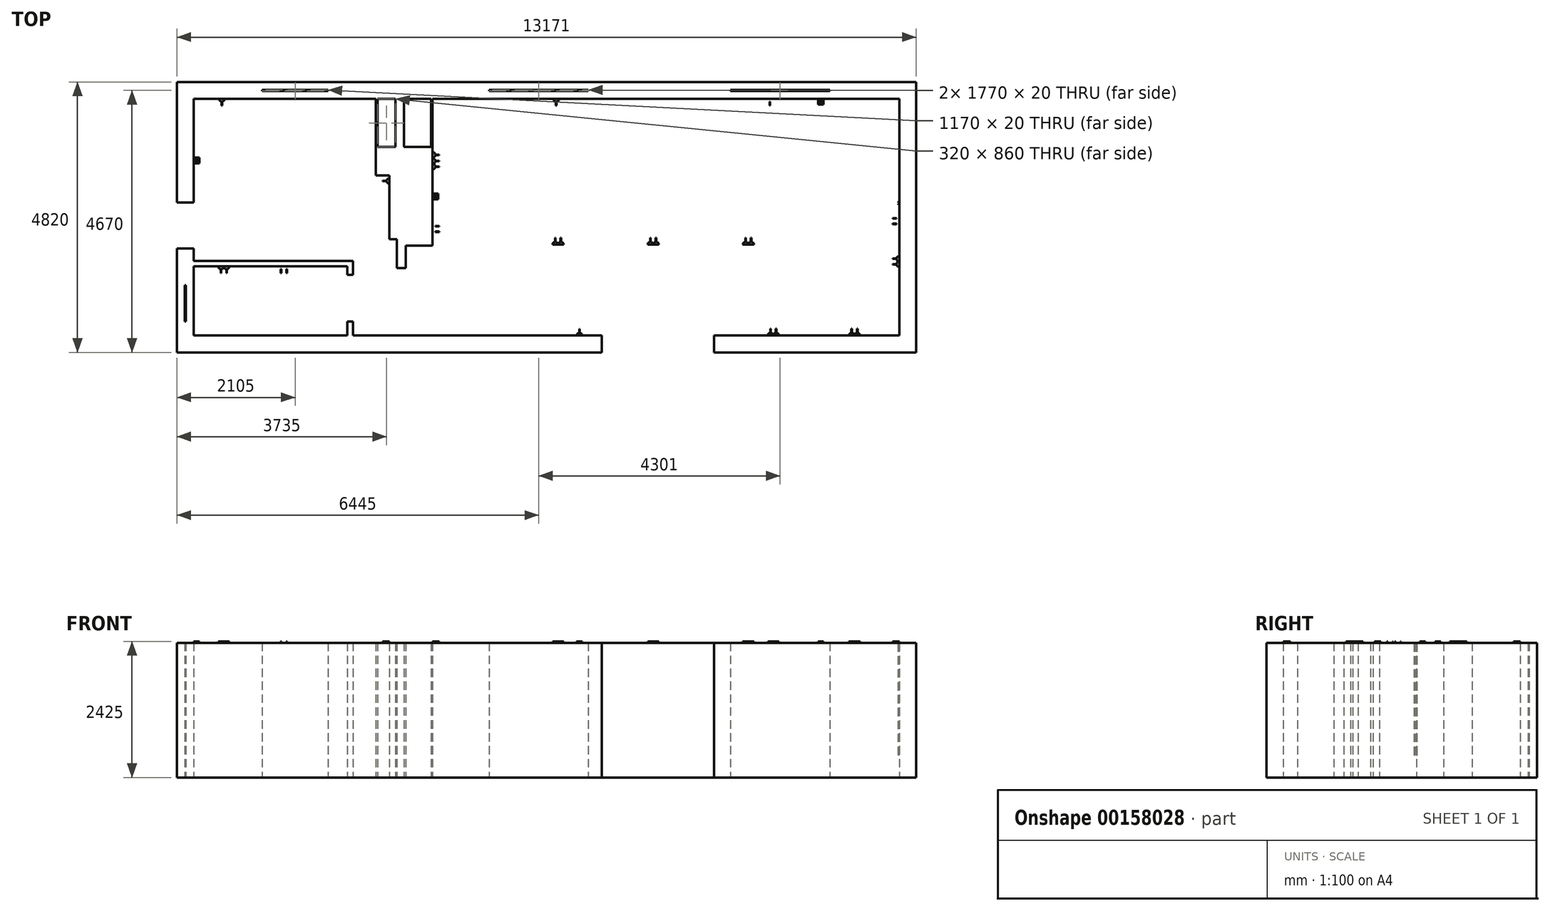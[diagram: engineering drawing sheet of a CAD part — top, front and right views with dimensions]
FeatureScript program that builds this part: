
annotation { "Feature Type Name" : "Feature", "Feature Type Description" : "" }
export const myFeature = defineFeature(function(context is Context, id is Id, definition is map)
    precondition{}
    {
        {
            var Q0;
            Q0=qCreatedBy(makeId("Top.planeOp"),FACE);
            var sketch = newSketch(context, id + "F0", { "sketchPlane" : qUnion([Q0])});
            skLineSegment(sketch, "E0", {"start": v(-4269.88, 1654.6) * mm, "end": v(-3049.88, 1654.6) * mm});
            skLineSegment(sketch, "E1", {"start": v(-3049.88, 1654.6) * mm, "end": v(-3049.88, 1954.6) * mm});
            skLineSegment(sketch, "E2", {"start": v(-3049.88, 1954.6) * mm, "end": v(-4569.88, 1954.6) * mm});
            skLineSegment(sketch, "E3", {"start": v(-4569.88, 1954.6) * mm, "end": v(-4569.88, -195.4) * mm});
            skLineSegment(sketch, "E4", {"start": v(-4569.88, -195.4) * mm, "end": v(-4269.88, -195.4) * mm});
            skLineSegment(sketch, "E5", {"start": v(-4269.88, -195.4) * mm, "end": v(-4269.88, 1654.6) * mm});
            skLineSegment(sketch, "E6", {"start": v(-674.88, 794.6) * mm, "end": v(-674.88, 1654.6) * mm});
            skLineSegment(sketch, "E7", {"start": v(-674.88, 1654.6) * mm, "end": v(-1879.88, 1654.6) * mm});
            skLineSegment(sketch, "E8", {"start": v(-1879.88, 1654.6) * mm, "end": v(-1879.88, 1954.6) * mm});
            skLineSegment(sketch, "E9", {"start": v(-1879.88, 1954.6) * mm, "end": v(990.12, 1954.6) * mm});
            skLineSegment(sketch, "E10", {"start": v(990.12, 1954.6) * mm, "end": v(990.12, 1654.6) * mm});
            skLineSegment(sketch, "E11", {"start": v(990.12, 1654.6) * mm, "end": v(-524.88, 1654.6) * mm});
            skLineSegment(sketch, "E12", {"start": v(-524.88, 1654.6) * mm, "end": v(-524.88, 794.6) * mm});
            skLineSegment(sketch, "E13", {"start": v(-674.88, 794.6) * mm, "end": v(-1024.88, 794.6) * mm});
            skLineSegment(sketch, "E14", {"start": v(-1024.88, 794.6) * mm, "end": v(-1024.88, 289.6) * mm});
            skLineSegment(sketch, "E15", {"start": v(-1024.88, 289.6) * mm, "end": v(-784.88, 289.6) * mm});
            skLineSegment(sketch, "E16", {"start": v(-784.88, 289.6) * mm, "end": v(-784.88, -850.4) * mm});
            skLineSegment(sketch, "E17", {"start": v(-784.88, -850.4) * mm, "end": v(-654.88, -850.4) * mm});
            skLineSegment(sketch, "E18", {"start": v(-654.88, -850.4) * mm, "end": v(-654.88, -1365.4) * mm});
            skLineSegment(sketch, "E19", {"start": v(-654.88, -1365.4) * mm, "end": v(-494.88, -1365.4) * mm});
            skLineSegment(sketch, "E20", {"start": v(-494.88, -1365.4) * mm, "end": v(-494.88, -965.4) * mm});
            skLineSegment(sketch, "E21", {"start": v(-494.88, -965.4) * mm, "end": v(-14.88, -965.4) * mm});
            skLineSegment(sketch, "E22", {"start": v(-14.88, -965.4) * mm, "end": v(-14.88, 794.6) * mm});
            skLineSegment(sketch, "E23", {"start": v(-14.88, 794.6) * mm, "end": v(-524.88, 794.6) * mm});
            skLineSegment(sketch, "E24", {"start": v(-4569.88, -1015.4) * mm, "end": v(-4269.88, -1015.4) * mm});
            skLineSegment(sketch, "E25", {"start": v(-4269.88, -1015.4) * mm, "end": v(-4269.88, -1235.4) * mm});
            skLineSegment(sketch, "E26", {"start": v(-4269.88, -1235.4) * mm, "end": v(-1435.88, -1235.4) * mm});
            skLineSegment(sketch, "E27", {"start": v(-1435.88, -1235.4) * mm, "end": v(-1435.88, -1485.4) * mm});
            skLineSegment(sketch, "E28", {"start": v(-1435.88, -1485.4) * mm, "end": v(-1532.88, -1485.4) * mm});
            skLineSegment(sketch, "E29", {"start": v(-1532.88, -1485.4) * mm, "end": v(-1532.88, -1332.4) * mm});
            skLineSegment(sketch, "E30", {"start": v(-1532.88, -1332.4) * mm, "end": v(-4269.88, -1332.4) * mm});
            skLineSegment(sketch, "E31", {"start": v(-4269.88, -1332.4) * mm, "end": v(-4269.88, -1665.4) * mm});
            skLineSegment(sketch, "E32", {"start": v(-4269.88, -1665.4) * mm, "end": v(-4569.88, -1665.4) * mm});
            skLineSegment(sketch, "E33", {"start": v(-4569.88, -1665.4) * mm, "end": v(-4569.88, -1015.4) * mm});
            skLineSegment(sketch, "E34", {"start": v(-4269.88, -2315.4) * mm, "end": v(-4269.88, -2565.4) * mm});
            skLineSegment(sketch, "E35", {"start": v(-4269.88, -2565.4) * mm, "end": v(-1532.88, -2565.4) * mm});
            skLineSegment(sketch, "E36", {"start": v(-1532.88, -2565.4) * mm, "end": v(-1532.88, -2315.4) * mm});
            skLineSegment(sketch, "E37", {"start": v(-1532.88, -2315.4) * mm, "end": v(-1435.88, -2315.4) * mm});
            skLineSegment(sketch, "E38", {"start": v(-1435.88, -2315.4) * mm, "end": v(-1435.88, -2565.4) * mm});
            skLineSegment(sketch, "E39", {"start": v(-4269.88, -2315.4) * mm, "end": v(-4569.88, -2315.4) * mm});
            skLineSegment(sketch, "E40", {"start": v(-4569.88, -2315.4) * mm, "end": v(-4569.88, -2865.4) * mm});
            skLineSegment(sketch, "E41", {"start": v(-4569.88, -2865.4) * mm, "end": v(3001.12, -2865.4) * mm});
            skLineSegment(sketch, "E42", {"start": v(3001.12, -2865.4) * mm, "end": v(3001.12, -2565.4) * mm});
            skLineSegment(sketch, "E43", {"start": v(3001.12, -2565.4) * mm, "end": v(-1435.88, -2565.4) * mm});
            skLineSegment(sketch, "E44", {"start": v(2760.12, 1954.6) * mm, "end": v(5291.12, 1954.6) * mm});
            skLineSegment(sketch, "E45", {"start": v(5291.12, 1954.6) * mm, "end": v(5291.12, 1654.6) * mm});
            skLineSegment(sketch, "E46", {"start": v(5291.12, 1654.6) * mm, "end": v(2760.12, 1654.6) * mm});
            skLineSegment(sketch, "E47", {"start": v(2760.12, 1654.6) * mm, "end": v(2760.12, 1954.6) * mm});
            skLineSegment(sketch, "E48", {"start": v(7061.12, 1954.6) * mm, "end": v(7061.12, 1654.6) * mm});
            skLineSegment(sketch, "E49", {"start": v(7061.12, 1654.6) * mm, "end": v(8301.12, 1654.6) * mm});
            skLineSegment(sketch, "E50", {"start": v(8301.12, 1654.6) * mm, "end": v(8301.12, -2565.4) * mm});
            skLineSegment(sketch, "E51", {"start": v(8301.12, -2565.4) * mm, "end": v(5001.12, -2565.4) * mm});
            skLineSegment(sketch, "E52", {"start": v(5001.12, -2565.4) * mm, "end": v(5001.12, -2865.4) * mm});
            skLineSegment(sketch, "E53", {"start": v(5001.12, -2865.4) * mm, "end": v(8601.12, -2865.4) * mm});
            skLineSegment(sketch, "E54", {"start": v(8601.12, -2865.4) * mm, "end": v(8601.12, 1954.6) * mm});
            skLineSegment(sketch, "E55", {"start": v(8601.12, 1954.6) * mm, "end": v(7061.12, 1954.6) * mm});
            skLineSegment(sketch, "E56", {"start": v(-3049.88, 1954.6) * mm, "end": v(-1879.88, 1954.6) * mm});
            skLineSegment(sketch, "E57", {"start": v(-3049.88, 1654.6) * mm, "end": v(-1879.88, 1654.6) * mm});
            skLineSegment(sketch, "E58", {"start": v(990.12, 1954.6) * mm, "end": v(2760.12, 1954.6) * mm});
            skLineSegment(sketch, "E59", {"start": v(990.12, 1654.6) * mm, "end": v(2760.12, 1654.6) * mm});
            skLineSegment(sketch, "E60", {"start": v(5291.12, 1654.6) * mm, "end": v(7061.12, 1654.6) * mm});
            skLineSegment(sketch, "E61", {"start": v(5291.12, 1954.6) * mm, "end": v(7061.12, 1954.6) * mm});
            skLineSegment(sketch, "E62", {"start": v(-3049.88, 1814.6) * mm, "end": v(-1879.88, 1814.6) * mm});
            skLineSegment(sketch, "E63", {"start": v(-3049.88, 1794.6) * mm, "end": v(-1879.88, 1794.6) * mm});
            skLineSegment(sketch, "E64", {"start": v(990.12, 1814.6) * mm, "end": v(2760.12, 1814.6) * mm});
            skLineSegment(sketch, "E65", {"start": v(990.12, 1794.6) * mm, "end": v(2760.12, 1794.6) * mm});
            skLineSegment(sketch, "E66", {"start": v(5291.12, 1814.6) * mm, "end": v(7061.12, 1814.6) * mm});
            skPoint(sketch, "E66.endSnap0", {"position": v(7061.12, 1804.6) * mm});
            skLineSegment(sketch, "E67", {"start": v(5291.12, 1794.6) * mm, "end": v(7061.12, 1794.6) * mm});
            skLineSegment(sketch, "E68", {"start": v(-4269.88, -1665.4) * mm, "end": v(-4269.88, -2315.4) * mm});
            skLineSegment(sketch, "E69", {"start": v(-4569.88, -1665.4) * mm, "end": v(-4569.88, -2315.4) * mm});
            skLineSegment(sketch, "E70", {"start": v(-4429.88, -1665.4) * mm, "end": v(-4429.88, -2315.4) * mm});
            skLineSegment(sketch, "E71", {"start": v(-4409.88, -1665.4) * mm, "end": v(-4409.88, -2315.4) * mm});
            skLineSegment(sketch, "E72", {"start": v(-1024.88, 794.6) * mm, "end": v(-1024.88, 1654.6) * mm});
            skLineSegment(sketch, "E73", {"start": v(-994.88, 794.6) * mm, "end": v(-994.88, 1654.6) * mm});
            skLineSegment(sketch, "E74", {"start": v(-14.88, 794.6) * mm, "end": v(-14.88, 1654.6) * mm});
            skLineSegment(sketch, "E75", {"start": v(-44.88, 794.6) * mm, "end": v(-44.88, 1654.6) * mm});
            skSolve(sketch);
        }
        {
            var Q0;
            {var subQ4=sQuery(id+"F0.wireOp",EDGE,"E0");Q0=makeQuery(id+"F0.imprint","IMPRINT",FACE,{"disambiguationData":[TD([[makeQuery(id+"F0.imprint","IMPRINT",EDGE,{"derivedFrom":subQ4}),1.0]])]});}
            var Q1;
            {var subQ0=sQuery(id+"F0.wireOp",EDGE,"E57");Q1=makeQuery(id+"F0.imprint","IMPRINT",FACE,{"disambiguationData":[TD([[makeQuery(id+"F0.imprint","IMPRINT",EDGE,{"derivedFrom":subQ0}),1.0]])]});}
            var Q2;
            {var subQ0=sQuery(id+"F0.wireOp",EDGE,"E56");Q2=makeQuery(id+"F0.imprint","IMPRINT",FACE,{"disambiguationData":[TD([[makeQuery(id+"F0.imprint","IMPRINT",EDGE,{"derivedFrom":subQ0}),-1.0]])]});}
            var Q3;
            {var subQ6=sQuery(id+"F0.wireOp",EDGE,"E6");Q3=makeQuery(id+"F0.imprint","IMPRINT",FACE,{"disambiguationData":[TD([[makeQuery(id+"F0.imprint","IMPRINT",EDGE,{"derivedFrom":subQ6}),-1.0]])]});}
            var Q4;
            {var subQ0=sQuery(id+"F0.wireOp",EDGE,"E72");Q4=makeQuery(id+"F0.imprint","IMPRINT",FACE,{"disambiguationData":[TD([[makeQuery(id+"F0.imprint","IMPRINT",EDGE,{"derivedFrom":subQ0}),-1.0]])]});}
            var Q5;
            {var subQ0=sQuery(id+"F0.wireOp",EDGE,"E74");Q5=makeQuery(id+"F0.imprint","IMPRINT",FACE,{"disambiguationData":[TD([[makeQuery(id+"F0.imprint","IMPRINT",EDGE,{"derivedFrom":subQ0}),1.0]])]});}
            var Q6;
            {var subQ0=sQuery(id+"F0.wireOp",EDGE,"E59");Q6=makeQuery(id+"F0.imprint","IMPRINT",FACE,{"disambiguationData":[TD([[makeQuery(id+"F0.imprint","IMPRINT",EDGE,{"derivedFrom":subQ0}),1.0]])]});}
            var Q7;
            {var subQ0=sQuery(id+"F0.wireOp",EDGE,"E58");Q7=makeQuery(id+"F0.imprint","IMPRINT",FACE,{"disambiguationData":[TD([[makeQuery(id+"F0.imprint","IMPRINT",EDGE,{"derivedFrom":subQ0}),-1.0]])]});}
            var Q8;
            {var subQ4=sQuery(id+"F0.wireOp",EDGE,"E44");Q8=makeQuery(id+"F0.imprint","IMPRINT",FACE,{"disambiguationData":[TD([[makeQuery(id+"F0.imprint","IMPRINT",EDGE,{"derivedFrom":subQ4}),-1.0]])]});}
            var Q9;
            {var subQ0=sQuery(id+"F0.wireOp",EDGE,"E60");Q9=makeQuery(id+"F0.imprint","IMPRINT",FACE,{"disambiguationData":[TD([[makeQuery(id+"F0.imprint","IMPRINT",EDGE,{"derivedFrom":subQ0}),1.0]])]});}
            var Q10;
            {var subQ0=sQuery(id+"F0.wireOp",EDGE,"E61");Q10=makeQuery(id+"F0.imprint","IMPRINT",FACE,{"disambiguationData":[TD([[makeQuery(id+"F0.imprint","IMPRINT",EDGE,{"derivedFrom":subQ0}),-1.0]])]});}
            var Q11;
            {var subQ0=sQuery(id+"F0.wireOp",EDGE,"E49");Q11=makeQuery(id+"F0.imprint","IMPRINT",FACE,{"disambiguationData":[TD([[makeQuery(id+"F0.imprint","IMPRINT",EDGE,{"derivedFrom":subQ0}),1.0]])]});}
            var Q12;
            {var subQ4=sQuery(id+"F0.wireOp",EDGE,"E34");Q12=makeQuery(id+"F0.imprint","IMPRINT",FACE,{"disambiguationData":[TD([[makeQuery(id+"F0.imprint","IMPRINT",EDGE,{"derivedFrom":subQ4}),-1.0]])]});}
            var Q13;
            {var subQ0=sQuery(id+"F0.wireOp",EDGE,"E68");Q13=makeQuery(id+"F0.imprint","IMPRINT",FACE,{"disambiguationData":[TD([[makeQuery(id+"F0.imprint","IMPRINT",EDGE,{"derivedFrom":subQ0}),-1.0]])]});}
            var Q14;
            {var subQ0=sQuery(id+"F0.wireOp",EDGE,"E69");Q14=makeQuery(id+"F0.imprint","IMPRINT",FACE,{"disambiguationData":[TD([[makeQuery(id+"F0.imprint","IMPRINT",EDGE,{"derivedFrom":subQ0}),1.0]])]});}
            var Q15;
            Q15=makeQuery(id+"F0.imprint","IMPRINT",FACE,{"disambiguationData":[TD([[makeQuery(id+"F0.imprint","IMPRINT",EDGE,{"derivedFrom":sQuery(id+"F0.wireOp",EDGE,"E24")}),-1.0]])]});
            extrude(context, id + "F1", {"entities" : qUnion([Q0, Q1, Q2, Q3, Q4, Q5, Q6, Q7, Q8, Q9, Q10, Q11, Q12, Q13, Q14, Q15]), "depth" : 2400 * mm});
        }
        {
            var Q0;
            Q0=makeQuery(id+"F1.opExtrude","CAP_FACE",FACE,{"disambiguationData":[OSD([sQuery(id+"F0.wireOp",EDGE,"E0"),sQuery(id+"F0.wireOp",EDGE,"E1"),sQuery(id+"F0.wireOp",EDGE,"E2"),sQuery(id+"F0.wireOp",EDGE,"E3"),sQuery(id+"F0.wireOp",EDGE,"E4"),sQuery(id+"F0.wireOp",EDGE,"E5"),sQuery(id+"F0.wireOp",EDGE,"E6"),sQuery(id+"F0.wireOp",EDGE,"E7"),sQuery(id+"F0.wireOp",EDGE,"E8"),sQuery(id+"F0.wireOp",EDGE,"E9"),sQuery(id+"F0.wireOp",EDGE,"E10"),sQuery(id+"F0.wireOp",EDGE,"E11"),sQuery(id+"F0.wireOp",EDGE,"E12"),sQuery(id+"F0.wireOp",EDGE,"E13"),sQuery(id+"F0.wireOp",EDGE,"E14"),sQuery(id+"F0.wireOp",EDGE,"E15"),sQuery(id+"F0.wireOp",EDGE,"E16"),sQuery(id+"F0.wireOp",EDGE,"E17"),sQuery(id+"F0.wireOp",EDGE,"E18"),sQuery(id+"F0.wireOp",EDGE,"E19"),sQuery(id+"F0.wireOp",EDGE,"E20"),sQuery(id+"F0.wireOp",EDGE,"E21"),sQuery(id+"F0.wireOp",EDGE,"E22"),sQuery(id+"F0.wireOp",EDGE,"E23"),sQuery(id+"F0.wireOp",EDGE,"E44"),sQuery(id+"F0.wireOp",EDGE,"E45"),sQuery(id+"F0.wireOp",EDGE,"E46"),sQuery(id+"F0.wireOp",EDGE,"E47"),sQuery(id+"F0.wireOp",EDGE,"E48"),sQuery(id+"F0.wireOp",EDGE,"E49"),sQuery(id+"F0.wireOp",EDGE,"E50"),sQuery(id+"F0.wireOp",EDGE,"E51"),sQuery(id+"F0.wireOp",EDGE,"E52"),sQuery(id+"F0.wireOp",EDGE,"E53"),sQuery(id+"F0.wireOp",EDGE,"E54"),sQuery(id+"F0.wireOp",EDGE,"E55"),sQuery(id+"F0.wireOp",EDGE,"E56"),sQuery(id+"F0.wireOp",EDGE,"E57"),sQuery(id+"F0.wireOp",EDGE,"E58"),sQuery(id+"F0.wireOp",EDGE,"E59"),sQuery(id+"F0.wireOp",EDGE,"E60"),sQuery(id+"F0.wireOp",EDGE,"E61"),sQuery(id+"F0.wireOp",EDGE,"E62"),sQuery(id+"F0.wireOp",EDGE,"E63"),sQuery(id+"F0.wireOp",EDGE,"E64"),sQuery(id+"F0.wireOp",EDGE,"E65"),sQuery(id+"F0.wireOp",EDGE,"E66"),sQuery(id+"F0.wireOp",EDGE,"E67"),sQuery(id+"F0.wireOp",EDGE,"E72"),sQuery(id+"F0.wireOp",EDGE,"E73"),sQuery(id+"F0.wireOp",EDGE,"E74"),sQuery(id+"F0.wireOp",EDGE,"E75")])],"isStart":false});
            var sketch = newSketch(context, id + "F2", { "sketchPlane" : qUnion([Q0])});
            skCircle(sketch, "E76", {"center": v(8291.12, -185.4) * mm, "radius": 7.5 * mm});
            skCircle(sketch, "E77", {"center": v(8291.12, -225.4) * mm, "radius": 7.5 * mm});
            skSolve(sketch);
        }
        {
            var Q0;
            Q0 = qSketchRegion(id + "F2", true);
            extrude(context, id + "F3", {"entities" : qUnion([Q0]), "oppositeDirection" : true, "depth" : 2000 * mm});
        }
        {
            var Q0;
            Q0=makeQuery(id+"F1.opExtrude","CAP_FACE",FACE,{"disambiguationData":[OSD([sQuery(id+"F0.wireOp",EDGE,"E0"),sQuery(id+"F0.wireOp",EDGE,"E1"),sQuery(id+"F0.wireOp",EDGE,"E2"),sQuery(id+"F0.wireOp",EDGE,"E3"),sQuery(id+"F0.wireOp",EDGE,"E4"),sQuery(id+"F0.wireOp",EDGE,"E5"),sQuery(id+"F0.wireOp",EDGE,"E6"),sQuery(id+"F0.wireOp",EDGE,"E7"),sQuery(id+"F0.wireOp",EDGE,"E8"),sQuery(id+"F0.wireOp",EDGE,"E9"),sQuery(id+"F0.wireOp",EDGE,"E10"),sQuery(id+"F0.wireOp",EDGE,"E11"),sQuery(id+"F0.wireOp",EDGE,"E12"),sQuery(id+"F0.wireOp",EDGE,"E13"),sQuery(id+"F0.wireOp",EDGE,"E14"),sQuery(id+"F0.wireOp",EDGE,"E15"),sQuery(id+"F0.wireOp",EDGE,"E16"),sQuery(id+"F0.wireOp",EDGE,"E17"),sQuery(id+"F0.wireOp",EDGE,"E18"),sQuery(id+"F0.wireOp",EDGE,"E19"),sQuery(id+"F0.wireOp",EDGE,"E20"),sQuery(id+"F0.wireOp",EDGE,"E21"),sQuery(id+"F0.wireOp",EDGE,"E22"),sQuery(id+"F0.wireOp",EDGE,"E23"),sQuery(id+"F0.wireOp",EDGE,"E44"),sQuery(id+"F0.wireOp",EDGE,"E45"),sQuery(id+"F0.wireOp",EDGE,"E46"),sQuery(id+"F0.wireOp",EDGE,"E47"),sQuery(id+"F0.wireOp",EDGE,"E48"),sQuery(id+"F0.wireOp",EDGE,"E49"),sQuery(id+"F0.wireOp",EDGE,"E50"),sQuery(id+"F0.wireOp",EDGE,"E51"),sQuery(id+"F0.wireOp",EDGE,"E52"),sQuery(id+"F0.wireOp",EDGE,"E53"),sQuery(id+"F0.wireOp",EDGE,"E54"),sQuery(id+"F0.wireOp",EDGE,"E55"),sQuery(id+"F0.wireOp",EDGE,"E56"),sQuery(id+"F0.wireOp",EDGE,"E57"),sQuery(id+"F0.wireOp",EDGE,"E58"),sQuery(id+"F0.wireOp",EDGE,"E59"),sQuery(id+"F0.wireOp",EDGE,"E60"),sQuery(id+"F0.wireOp",EDGE,"E61"),sQuery(id+"F0.wireOp",EDGE,"E62"),sQuery(id+"F0.wireOp",EDGE,"E63"),sQuery(id+"F0.wireOp",EDGE,"E64"),sQuery(id+"F0.wireOp",EDGE,"E65"),sQuery(id+"F0.wireOp",EDGE,"E66"),sQuery(id+"F0.wireOp",EDGE,"E67"),sQuery(id+"F0.wireOp",EDGE,"E72"),sQuery(id+"F0.wireOp",EDGE,"E73"),sQuery(id+"F0.wireOp",EDGE,"E74"),sQuery(id+"F0.wireOp",EDGE,"E75")])],"isStart":false});
            var sketch = newSketch(context, id + "F4", { "sketchPlane" : qUnion([Q0])});
            skArc(sketch, "E78", {"start": v(-3496.7, 1266.48) * mm, "mid": v(-3546.7, 1316.48) * mm, "end": v(-3596.7, 1266.48) * mm});
            skLineSegment(sketch, "E79", {"start": v(-3551.7, 1316.23) * mm, "end": v(-3551.7, 1391.23) * mm});
            skLineSegment(sketch, "E80", {"start": v(-3551.7, 1391.23) * mm, "end": v(-3541.7, 1391.23) * mm});
            skLineSegment(sketch, "E81", {"start": v(-3541.7, 1391.23) * mm, "end": v(-3541.7, 1316.23) * mm});
            skLineSegment(sketch, "E82", {"start": v(-3596.7, 1266.48) * mm, "end": v(-3496.7, 1266.48) * mm});
            skLineSegment(sketch, "E83", {"start": v(-3662.17, 1241.79) * mm, "end": v(-3369.84, 1241.79) * mm, "construction": true});
            skLineSegment(sketch, "E84.MirrorCS", {"start": v(-3551.7, 1092.34) * mm, "end": v(-3541.7, 1092.34) * mm});
            skLineSegment(sketch, "E85.MirrorCS", {"start": v(-3551.7, 1167.34) * mm, "end": v(-3551.7, 1092.34) * mm});
            skArc(sketch, "E86.MirrorCS", {"start": v(-3496.7, 1217.1) * mm, "mid": v(-3546.7, 1167.1) * mm, "end": v(-3596.7, 1217.1) * mm});
            skLineSegment(sketch, "E87.MirrorCS", {"start": v(-3541.7, 1092.34) * mm, "end": v(-3541.7, 1167.34) * mm});
            skLineSegment(sketch, "E88.MirrorCS", {"start": v(-3596.7, 1217.1) * mm, "end": v(-3496.7, 1217.1) * mm});
            skArc(sketch, "E89", {"start": v(6055.12, -2565.4) * mm, "mid": v(6005.12, -2515.4) * mm, "end": v(5955.12, -2565.4) * mm});
            skLineSegment(sketch, "E90", {"start": v(6000.12, -2515.65) * mm, "end": v(6000.12, -2440.65) * mm});
            skLineSegment(sketch, "E91", {"start": v(6000.12, -2440.65) * mm, "end": v(6010.12, -2440.65) * mm});
            skLineSegment(sketch, "E92", {"start": v(6010.12, -2440.65) * mm, "end": v(6010.12, -2515.65) * mm});
            skLineSegment(sketch, "E93", {"start": v(5955.12, -2565.4) * mm, "end": v(6055.12, -2565.4) * mm});
            skLineSegment(sketch, "E94", {"start": v(6055.12, -2565.4) * mm, "end": v(6055.12, -2326.2) * mm, "construction": true});
            skLineSegment(sketch, "E95.MirrorCS", {"start": v(6110.12, -2515.65) * mm, "end": v(6110.12, -2440.65) * mm});
            skArc(sketch, "E96.MirrorCS", {"start": v(6055.12, -2565.4) * mm, "mid": v(6105.12, -2515.4) * mm, "end": v(6155.12, -2565.4) * mm});
            skLineSegment(sketch, "E97.MirrorCS", {"start": v(6110.12, -2440.65) * mm, "end": v(6100.12, -2440.65) * mm});
            skLineSegment(sketch, "E98.MirrorCS", {"start": v(6100.12, -2440.65) * mm, "end": v(6100.12, -2515.65) * mm});
            skLineSegment(sketch, "E99.MirrorCS", {"start": v(6155.12, -2565.4) * mm, "end": v(6055.12, -2565.4) * mm});
            skArc(sketch, "E100", {"start": v(7501.12, -2565.4) * mm, "mid": v(7451.12, -2515.4) * mm, "end": v(7401.12, -2565.4) * mm});
            skLineSegment(sketch, "E101", {"start": v(7446.12, -2515.65) * mm, "end": v(7446.12, -2440.65) * mm});
            skLineSegment(sketch, "E102", {"start": v(7446.12, -2440.65) * mm, "end": v(7456.12, -2440.65) * mm});
            skLineSegment(sketch, "E103", {"start": v(7456.12, -2440.65) * mm, "end": v(7456.12, -2515.65) * mm});
            skLineSegment(sketch, "E104", {"start": v(7401.12, -2565.4) * mm, "end": v(7501.12, -2565.4) * mm});
            skLineSegment(sketch, "E105", {"start": v(7501.12, -2565.4) * mm, "end": v(7501.12, -2376.29) * mm, "construction": true});
            skLineSegment(sketch, "E106.MirrorCS", {"start": v(7556.12, -2440.65) * mm, "end": v(7546.12, -2440.65) * mm});
            skLineSegment(sketch, "E107.MirrorCS", {"start": v(7601.12, -2565.4) * mm, "end": v(7501.12, -2565.4) * mm});
            skArc(sketch, "E108.MirrorCS", {"start": v(7501.12, -2565.4) * mm, "mid": v(7551.12, -2515.4) * mm, "end": v(7601.12, -2565.4) * mm});
            skLineSegment(sketch, "E109.MirrorCS", {"start": v(7546.12, -2440.65) * mm, "end": v(7546.12, -2515.65) * mm});
            skLineSegment(sketch, "E110.MirrorCS", {"start": v(7556.12, -2515.65) * mm, "end": v(7556.12, -2440.65) * mm});
            skSolve(sketch);
        }
        {
            var Q0;
            {var subQ0=sQuery(id+"F4.wireOp",EDGE,"E93");Q0=makeQuery(id+"F4.imprint","IMPRINT",FACE,{"disambiguationData":[TD([[makeQuery(id+"F4.imprint","IMPRINT",EDGE,{"derivedFrom":subQ0}),-1.0]])]});}
            var Q1;
            {var subQ0=sQuery(id+"F4.wireOp",EDGE,"E99.MirrorCS");Q1=makeQuery(id+"F4.imprint","IMPRINT",FACE,{"disambiguationData":[TD([[makeQuery(id+"F4.imprint","IMPRINT",EDGE,{"derivedFrom":subQ0}),-1.0]])]});}
            var Q2;
            {var subQ0=sQuery(id+"F4.wireOp",EDGE,"E104");Q2=makeQuery(id+"F4.imprint","IMPRINT",FACE,{"disambiguationData":[TD([[makeQuery(id+"F4.imprint","IMPRINT",EDGE,{"derivedFrom":subQ0}),-1.0]])]});}
            var Q3;
            {var subQ0=sQuery(id+"F4.wireOp",EDGE,"E107.MirrorCS");Q3=makeQuery(id+"F4.imprint","IMPRINT",FACE,{"disambiguationData":[TD([[makeQuery(id+"F4.imprint","IMPRINT",EDGE,{"derivedFrom":subQ0}),-1.0]])]});}
            extrude(context, id + "F5", {"entities" : qUnion([Q0, Q1, Q2, Q3]), "depth" : 25 * mm});
        }
        {
            var Q0;
            {var subQ0=sQuery(id+"F4.wireOp",EDGE,"E90");Q0=makeQuery(id+"F4.imprint","IMPRINT",FACE,{"disambiguationData":[TD([[makeQuery(id+"F4.imprint","IMPRINT",EDGE,{"derivedFrom":subQ0}),-1.0]])]});}
            var Q1;
            {var subQ0=sQuery(id+"F4.wireOp",EDGE,"E95.MirrorCS");Q1=makeQuery(id+"F4.imprint","IMPRINT",FACE,{"disambiguationData":[TD([[makeQuery(id+"F4.imprint","IMPRINT",EDGE,{"derivedFrom":subQ0}),1.0]])]});}
            var Q2;
            {var subQ0=sQuery(id+"F4.wireOp",EDGE,"E101");Q2=makeQuery(id+"F4.imprint","IMPRINT",FACE,{"disambiguationData":[TD([[makeQuery(id+"F4.imprint","IMPRINT",EDGE,{"derivedFrom":subQ0}),-1.0]])]});}
            var Q3;
            Q3=makeQuery(id+"F4.imprint","IMPRINT",FACE,{"disambiguationData":[TD([[makeQuery(id+"F4.imprint","IMPRINT",EDGE,{"derivedFrom":sQuery(id+"F4.wireOp",EDGE,"E106.MirrorCS")}),1.0]])]});
            extrude(context, id + "F6", {"entities" : qUnion([Q0, Q1, Q2, Q3]), "operationType" : NewBodyOperationType.ADD, "depth" : 24 * mm});
        }
        {
            var Q0;
            Q0=makeQuery(id+"F1.opExtrude","CAP_FACE",FACE,{"disambiguationData":[OSD([sQuery(id+"F0.wireOp",EDGE,"E0"),sQuery(id+"F0.wireOp",EDGE,"E1"),sQuery(id+"F0.wireOp",EDGE,"E2"),sQuery(id+"F0.wireOp",EDGE,"E3"),sQuery(id+"F0.wireOp",EDGE,"E4"),sQuery(id+"F0.wireOp",EDGE,"E5"),sQuery(id+"F0.wireOp",EDGE,"E6"),sQuery(id+"F0.wireOp",EDGE,"E7"),sQuery(id+"F0.wireOp",EDGE,"E8"),sQuery(id+"F0.wireOp",EDGE,"E9"),sQuery(id+"F0.wireOp",EDGE,"E10"),sQuery(id+"F0.wireOp",EDGE,"E11"),sQuery(id+"F0.wireOp",EDGE,"E12"),sQuery(id+"F0.wireOp",EDGE,"E13"),sQuery(id+"F0.wireOp",EDGE,"E14"),sQuery(id+"F0.wireOp",EDGE,"E15"),sQuery(id+"F0.wireOp",EDGE,"E16"),sQuery(id+"F0.wireOp",EDGE,"E17"),sQuery(id+"F0.wireOp",EDGE,"E18"),sQuery(id+"F0.wireOp",EDGE,"E19"),sQuery(id+"F0.wireOp",EDGE,"E20"),sQuery(id+"F0.wireOp",EDGE,"E21"),sQuery(id+"F0.wireOp",EDGE,"E22"),sQuery(id+"F0.wireOp",EDGE,"E23"),sQuery(id+"F0.wireOp",EDGE,"E44"),sQuery(id+"F0.wireOp",EDGE,"E45"),sQuery(id+"F0.wireOp",EDGE,"E46"),sQuery(id+"F0.wireOp",EDGE,"E47"),sQuery(id+"F0.wireOp",EDGE,"E48"),sQuery(id+"F0.wireOp",EDGE,"E49"),sQuery(id+"F0.wireOp",EDGE,"E50"),sQuery(id+"F0.wireOp",EDGE,"E51"),sQuery(id+"F0.wireOp",EDGE,"E52"),sQuery(id+"F0.wireOp",EDGE,"E53"),sQuery(id+"F0.wireOp",EDGE,"E54"),sQuery(id+"F0.wireOp",EDGE,"E55"),sQuery(id+"F0.wireOp",EDGE,"E56"),sQuery(id+"F0.wireOp",EDGE,"E57"),sQuery(id+"F0.wireOp",EDGE,"E58"),sQuery(id+"F0.wireOp",EDGE,"E59"),sQuery(id+"F0.wireOp",EDGE,"E60"),sQuery(id+"F0.wireOp",EDGE,"E61"),sQuery(id+"F0.wireOp",EDGE,"E62"),sQuery(id+"F0.wireOp",EDGE,"E63"),sQuery(id+"F0.wireOp",EDGE,"E64"),sQuery(id+"F0.wireOp",EDGE,"E65"),sQuery(id+"F0.wireOp",EDGE,"E66"),sQuery(id+"F0.wireOp",EDGE,"E67"),sQuery(id+"F0.wireOp",EDGE,"E72"),sQuery(id+"F0.wireOp",EDGE,"E73"),sQuery(id+"F0.wireOp",EDGE,"E74"),sQuery(id+"F0.wireOp",EDGE,"E75")])],"isStart":false});
            var sketch = newSketch(context, id + "F7", { "sketchPlane" : qUnion([Q0])});
            skArc(sketch, "E111", {"start": v(8301.12, -1245.4) * mm, "mid": v(8251.12, -1295.4) * mm, "end": v(8301.12, -1345.4) * mm});
            skArc(sketch, "E112", {"start": v(8301.12, -1145.4) * mm, "mid": v(8251.12, -1195.4) * mm, "end": v(8301.12, -1245.4) * mm});
            skLineSegment(sketch, "E113", {"start": v(8301.12, -1145.4) * mm, "end": v(8301.12, -1345.4) * mm});
            skLineSegment(sketch, "E114", {"start": v(8251.37, -1300.4) * mm, "end": v(8181.37, -1300.4) * mm});
            skLineSegment(sketch, "E115", {"start": v(8181.37, -1300.4) * mm, "end": v(8181.37, -1290.4) * mm});
            skLineSegment(sketch, "E116", {"start": v(8181.37, -1290.4) * mm, "end": v(8251.37, -1290.4) * mm});
            skLineSegment(sketch, "E117", {"start": v(8251.37, -1200.4) * mm, "end": v(8181.37, -1200.4) * mm});
            skLineSegment(sketch, "E118", {"start": v(8181.37, -1200.4) * mm, "end": v(8181.37, -1190.4) * mm});
            skLineSegment(sketch, "E119", {"start": v(8181.37, -1190.4) * mm, "end": v(8251.37, -1190.4) * mm});
            skLineSegment(sketch, "E120", {"start": v(8301.12, -885.4) * mm, "end": v(7281.12, -885.4) * mm, "construction": true});
            skLineSegment(sketch, "E121.MirrorCS", {"start": v(8181.37, -470.4) * mm, "end": v(8181.37, -480.4) * mm});
            skLineSegment(sketch, "E122.MirrorCS", {"start": v(8181.37, -570.4) * mm, "end": v(8181.37, -580.4) * mm});
            skLineSegment(sketch, "E123.MirrorCS", {"start": v(8301.12, -625.4) * mm, "end": v(8301.12, -425.4) * mm});
            skLineSegment(sketch, "E124.MirrorCS", {"start": v(8251.37, -470.4) * mm, "end": v(8181.37, -470.4) * mm});
            skArc(sketch, "E125.MirrorCS", {"start": v(8301.12, -625.4) * mm, "mid": v(8251.12, -575.4) * mm, "end": v(8301.12, -525.4) * mm});
            skArc(sketch, "E126.MirrorCS", {"start": v(8301.12, -525.4) * mm, "mid": v(8251.12, -475.4) * mm, "end": v(8301.12, -425.4) * mm});
            skLineSegment(sketch, "E127.MirrorCS", {"start": v(8181.37, -480.4) * mm, "end": v(8251.37, -480.4) * mm});
            skLineSegment(sketch, "E128.MirrorCS", {"start": v(8251.37, -570.4) * mm, "end": v(8181.37, -570.4) * mm});
            skLineSegment(sketch, "E129.MirrorCS", {"start": v(8181.37, -580.4) * mm, "end": v(8251.37, -580.4) * mm});
            skSolve(sketch);
        }
        {
            var Q0;
            {var subQ1=sQuery(id+"F7.wireOp",EDGE,"E111");var subQ4=makeQuery(id+"F7.imprint","INTERSECT",VERTEX,{"derivedFrom":[subQ1,sQuery(id+"F7.wireOp",EDGE,"E114")]});Q0=makeQuery(id+"F7.imprint","IMPRINT",FACE,{"disambiguationData":[TD([[makeQuery(id+"F7.imprint","IMPRINT",EDGE,{"disambiguationData":[TD([[subQ4,1.0]])],"derivedFrom":subQ1}),1.0]])]});}
            var Q1;
            {var subQ1=sQuery(id+"F7.wireOp",EDGE,"E112");var subQ4=makeQuery(id+"F7.imprint","INTERSECT",VERTEX,{"derivedFrom":[subQ1,sQuery(id+"F7.wireOp",EDGE,"E117")]});Q1=makeQuery(id+"F7.imprint","IMPRINT",FACE,{"disambiguationData":[TD([[makeQuery(id+"F7.imprint","IMPRINT",EDGE,{"disambiguationData":[TD([[subQ4,1.0]])],"derivedFrom":subQ1}),1.0]])]});}
            var Q2;
            {var subQ0=sQuery(id+"F7.wireOp",EDGE,"E125.MirrorCS");var subQ5=makeQuery(id+"F7.imprint","INTERSECT",VERTEX,{"derivedFrom":[subQ0,sQuery(id+"F7.wireOp",EDGE,"E128.MirrorCS")]});Q2=makeQuery(id+"F7.imprint","IMPRINT",FACE,{"disambiguationData":[TD([[makeQuery(id+"F7.imprint","IMPRINT",EDGE,{"disambiguationData":[TD([[subQ5,1.0]])],"derivedFrom":subQ0}),-1.0]])]});}
            var Q3;
            {var subQ0=sQuery(id+"F7.wireOp",EDGE,"E126.MirrorCS");var subQ5=makeQuery(id+"F7.imprint","INTERSECT",VERTEX,{"derivedFrom":[sQuery(id+"F7.wireOp",EDGE,"E124.MirrorCS"),subQ0]});Q3=makeQuery(id+"F7.imprint","IMPRINT",FACE,{"disambiguationData":[TD([[makeQuery(id+"F7.imprint","IMPRINT",EDGE,{"disambiguationData":[TD([[subQ5,1.0]])],"derivedFrom":subQ0}),-1.0]])]});}
            extrude(context, id + "F8", {"entities" : qUnion([Q0, Q1, Q2, Q3]), "depth" : 25 * mm});
        }
        {
            var Q0;
            Q0=makeQuery(id+"F7.imprint","IMPRINT",FACE,{"disambiguationData":[TD([[makeQuery(id+"F7.imprint","IMPRINT",EDGE,{"derivedFrom":sQuery(id+"F7.wireOp",EDGE,"E121.MirrorCS")}),1.0]])]});
            var Q1;
            Q1=makeQuery(id+"F7.imprint","IMPRINT",FACE,{"disambiguationData":[TD([[makeQuery(id+"F7.imprint","IMPRINT",EDGE,{"derivedFrom":sQuery(id+"F7.wireOp",EDGE,"E122.MirrorCS")}),1.0]])]});
            var Q2;
            {var subQ0=sQuery(id+"F7.wireOp",EDGE,"E117");Q2=makeQuery(id+"F7.imprint","IMPRINT",FACE,{"disambiguationData":[TD([[makeQuery(id+"F7.imprint","IMPRINT",EDGE,{"derivedFrom":subQ0}),-1.0]])]});}
            var Q3;
            {var subQ0=sQuery(id+"F7.wireOp",EDGE,"E114");Q3=makeQuery(id+"F7.imprint","IMPRINT",FACE,{"disambiguationData":[TD([[makeQuery(id+"F7.imprint","IMPRINT",EDGE,{"derivedFrom":subQ0}),-1.0]])]});}
            extrude(context, id + "F9", {"entities" : qUnion([Q0, Q1, Q2, Q3]), "operationType" : NewBodyOperationType.ADD, "depth" : 24 * mm});
        }
        {
            var Q0;
            Q0=makeQuery(id+"F1.opExtrude","CAP_FACE",FACE,{"disambiguationData":[OSD([sQuery(id+"F0.wireOp",EDGE,"E24"),sQuery(id+"F0.wireOp",EDGE,"E25"),sQuery(id+"F0.wireOp",EDGE,"E26"),sQuery(id+"F0.wireOp",EDGE,"E27"),sQuery(id+"F0.wireOp",EDGE,"E28"),sQuery(id+"F0.wireOp",EDGE,"E29"),sQuery(id+"F0.wireOp",EDGE,"E30"),sQuery(id+"F0.wireOp",EDGE,"E31"),sQuery(id+"F0.wireOp",EDGE,"E32"),sQuery(id+"F0.wireOp",EDGE,"E33"),sQuery(id+"F0.wireOp",EDGE,"E34"),sQuery(id+"F0.wireOp",EDGE,"E35"),sQuery(id+"F0.wireOp",EDGE,"E36"),sQuery(id+"F0.wireOp",EDGE,"E37"),sQuery(id+"F0.wireOp",EDGE,"E38"),sQuery(id+"F0.wireOp",EDGE,"E39"),sQuery(id+"F0.wireOp",EDGE,"E40"),sQuery(id+"F0.wireOp",EDGE,"E41"),sQuery(id+"F0.wireOp",EDGE,"E42"),sQuery(id+"F0.wireOp",EDGE,"E43"),sQuery(id+"F0.wireOp",EDGE,"E68"),sQuery(id+"F0.wireOp",EDGE,"E69"),sQuery(id+"F0.wireOp",EDGE,"E70"),sQuery(id+"F0.wireOp",EDGE,"E71")])],"isStart":false});
            var sketch = newSketch(context, id + "F10", { "sketchPlane" : qUnion([Q0])});
            skArc(sketch, "E130", {"start": v(-3834.88, -1332.4) * mm, "mid": v(-3784.88, -1382.4) * mm, "end": v(-3734.88, -1332.4) * mm});
            skArc(sketch, "E131", {"start": v(-3734.88, -1332.4) * mm, "mid": v(-3684.88, -1382.4) * mm, "end": v(-3634.88, -1332.4) * mm});
            skLineSegment(sketch, "E132", {"start": v(-3834.88, -1332.4) * mm, "end": v(-3634.88, -1332.4) * mm});
            skLineSegment(sketch, "E133", {"start": v(-3789.88, -1382.15) * mm, "end": v(-3789.88, -1452.15) * mm});
            skLineSegment(sketch, "E134", {"start": v(-3789.88, -1452.15) * mm, "end": v(-3779.88, -1452.15) * mm});
            skLineSegment(sketch, "E135", {"start": v(-3779.88, -1452.15) * mm, "end": v(-3779.88, -1382.15) * mm});
            skLineSegment(sketch, "E136", {"start": v(-3689.88, -1382.15) * mm, "end": v(-3689.88, -1452.15) * mm});
            skLineSegment(sketch, "E137", {"start": v(-3689.88, -1452.15) * mm, "end": v(-3679.88, -1452.15) * mm});
            skLineSegment(sketch, "E138", {"start": v(-3679.88, -1452.15) * mm, "end": v(-3679.88, -1382.15) * mm});
            skLineSegment(sketch, "E139", {"start": v(-3199.88, -1332.4) * mm, "end": v(-3199.88, -1501.65) * mm, "construction": true});
            skLineSegment(sketch, "E140.MirrorCS", {"start": v(-2709.88, -1452.15) * mm, "end": v(-2719.88, -1452.15) * mm});
            skLineSegment(sketch, "E141.MirrorCS", {"start": v(-2609.88, -1452.15) * mm, "end": v(-2619.88, -1452.15) * mm});
            skLineSegment(sketch, "E142.MirrorCS", {"start": v(-2719.88, -1452.15) * mm, "end": v(-2719.88, -1382.15) * mm});
            skLineSegment(sketch, "E143.MirrorCS", {"start": v(-2709.88, -1382.15) * mm, "end": v(-2709.88, -1452.15) * mm});
            skArc(sketch, "E144.MirrorCS", {"start": v(-2564.88, -1332.4) * mm, "mid": v(-2614.88, -1382.4) * mm, "end": v(-2664.88, -1332.4) * mm});
            skArc(sketch, "E145.MirrorCS", {"start": v(-2664.88, -1332.4) * mm, "mid": v(-2714.88, -1382.4) * mm, "end": v(-2764.88, -1332.4) * mm});
            skLineSegment(sketch, "E146.MirrorCS", {"start": v(-2609.88, -1382.15) * mm, "end": v(-2609.88, -1452.15) * mm});
            skLineSegment(sketch, "E147.MirrorCS", {"start": v(-2564.88, -1332.4) * mm, "end": v(-2764.88, -1332.4) * mm});
            skLineSegment(sketch, "E148.MirrorCS", {"start": v(-2619.88, -1452.15) * mm, "end": v(-2619.88, -1382.15) * mm});
            skSolve(sketch);
        }
        {
            var Q0;
            {var subQ1=sQuery(id+"F10.wireOp",EDGE,"E130");var subQ3=makeQuery(id+"F10.imprint","INTERSECT",VERTEX,{"derivedFrom":[subQ1,sQuery(id+"F10.wireOp",EDGE,"E133")]});Q0=makeQuery(id+"F10.imprint","IMPRINT",FACE,{"disambiguationData":[TD([[makeQuery(id+"F10.imprint","IMPRINT",EDGE,{"disambiguationData":[TD([[subQ3,-1.0]])],"derivedFrom":subQ1}),1.0]])]});}
            var Q1;
            {var subQ1=sQuery(id+"F10.wireOp",EDGE,"E131");var subQ3=makeQuery(id+"F10.imprint","INTERSECT",VERTEX,{"derivedFrom":[subQ1,sQuery(id+"F10.wireOp",EDGE,"E136")]});Q1=makeQuery(id+"F10.imprint","IMPRINT",FACE,{"disambiguationData":[TD([[makeQuery(id+"F10.imprint","IMPRINT",EDGE,{"disambiguationData":[TD([[subQ3,-1.0]])],"derivedFrom":subQ1}),1.0]])]});}
            var Q2;
            {var subQ0=sQuery(id+"F10.wireOp",EDGE,"E145.MirrorCS");var subQ4=makeQuery(id+"F10.imprint","INTERSECT",VERTEX,{"derivedFrom":[sQuery(id+"F10.wireOp",EDGE,"E142.MirrorCS"),subQ0]});Q2=makeQuery(id+"F10.imprint","IMPRINT",FACE,{"disambiguationData":[TD([[makeQuery(id+"F10.imprint","IMPRINT",EDGE,{"disambiguationData":[TD([[subQ4,1.0]])],"derivedFrom":subQ0}),-1.0]])]});}
            var Q3;
            {var subQ1=sQuery(id+"F10.wireOp",EDGE,"E144.MirrorCS");var subQ3=makeQuery(id+"F10.imprint","INTERSECT",VERTEX,{"derivedFrom":[subQ1,sQuery(id+"F10.wireOp",EDGE,"E146.MirrorCS")]});Q3=makeQuery(id+"F10.imprint","IMPRINT",FACE,{"disambiguationData":[TD([[makeQuery(id+"F10.imprint","IMPRINT",EDGE,{"disambiguationData":[TD([[subQ3,-1.0]])],"derivedFrom":subQ1}),-1.0]])]});}
            extrude(context, id + "F11", {"entities" : qUnion([Q0, Q1, Q2, Q3]), "depth" : 25 * mm});
        }
        {
            var Q0;
            {var subQ0=sQuery(id+"F10.wireOp",EDGE,"E136");Q0=makeQuery(id+"F10.imprint","IMPRINT",FACE,{"disambiguationData":[TD([[makeQuery(id+"F10.imprint","IMPRINT",EDGE,{"derivedFrom":subQ0}),1.0]])]});}
            var Q1;
            {var subQ0=sQuery(id+"F10.wireOp",EDGE,"E133");Q1=makeQuery(id+"F10.imprint","IMPRINT",FACE,{"disambiguationData":[TD([[makeQuery(id+"F10.imprint","IMPRINT",EDGE,{"derivedFrom":subQ0}),1.0]])]});}
            extrude(context, id + "F12", {"entities" : qUnion([Q0, Q1]), "operationType" : NewBodyOperationType.ADD, "depth" : 24 * mm});
        }
        {
            var Q0;
            Q0=makeQuery(id+"F10.imprint","IMPRINT",FACE,{"disambiguationData":[TD([[makeQuery(id+"F10.imprint","IMPRINT",EDGE,{"derivedFrom":sQuery(id+"F10.wireOp",EDGE,"E140.MirrorCS")}),-1.0]])]});
            var Q1;
            Q1=makeQuery(id+"F10.imprint","IMPRINT",FACE,{"disambiguationData":[TD([[makeQuery(id+"F10.imprint","IMPRINT",EDGE,{"derivedFrom":sQuery(id+"F10.wireOp",EDGE,"E141.MirrorCS")}),-1.0]])]});
            extrude(context, id + "F13", {"entities" : qUnion([Q0, Q1]), "operationType" : NewBodyOperationType.ADD, "depth" : 24 * mm});
        }
        {
            var Q0;
            Q0=makeQuery(id+"F1.opExtrude","CAP_FACE",FACE,{"disambiguationData":[OSD([sQuery(id+"F0.wireOp",EDGE,"E0"),sQuery(id+"F0.wireOp",EDGE,"E1"),sQuery(id+"F0.wireOp",EDGE,"E2"),sQuery(id+"F0.wireOp",EDGE,"E3"),sQuery(id+"F0.wireOp",EDGE,"E4"),sQuery(id+"F0.wireOp",EDGE,"E5"),sQuery(id+"F0.wireOp",EDGE,"E6"),sQuery(id+"F0.wireOp",EDGE,"E7"),sQuery(id+"F0.wireOp",EDGE,"E8"),sQuery(id+"F0.wireOp",EDGE,"E9"),sQuery(id+"F0.wireOp",EDGE,"E10"),sQuery(id+"F0.wireOp",EDGE,"E11"),sQuery(id+"F0.wireOp",EDGE,"E12"),sQuery(id+"F0.wireOp",EDGE,"E13"),sQuery(id+"F0.wireOp",EDGE,"E14"),sQuery(id+"F0.wireOp",EDGE,"E15"),sQuery(id+"F0.wireOp",EDGE,"E16"),sQuery(id+"F0.wireOp",EDGE,"E17"),sQuery(id+"F0.wireOp",EDGE,"E18"),sQuery(id+"F0.wireOp",EDGE,"E19"),sQuery(id+"F0.wireOp",EDGE,"E20"),sQuery(id+"F0.wireOp",EDGE,"E21"),sQuery(id+"F0.wireOp",EDGE,"E22"),sQuery(id+"F0.wireOp",EDGE,"E23"),sQuery(id+"F0.wireOp",EDGE,"E44"),sQuery(id+"F0.wireOp",EDGE,"E45"),sQuery(id+"F0.wireOp",EDGE,"E46"),sQuery(id+"F0.wireOp",EDGE,"E47"),sQuery(id+"F0.wireOp",EDGE,"E48"),sQuery(id+"F0.wireOp",EDGE,"E49"),sQuery(id+"F0.wireOp",EDGE,"E50"),sQuery(id+"F0.wireOp",EDGE,"E51"),sQuery(id+"F0.wireOp",EDGE,"E52"),sQuery(id+"F0.wireOp",EDGE,"E53"),sQuery(id+"F0.wireOp",EDGE,"E54"),sQuery(id+"F0.wireOp",EDGE,"E55"),sQuery(id+"F0.wireOp",EDGE,"E56"),sQuery(id+"F0.wireOp",EDGE,"E57"),sQuery(id+"F0.wireOp",EDGE,"E58"),sQuery(id+"F0.wireOp",EDGE,"E59"),sQuery(id+"F0.wireOp",EDGE,"E60"),sQuery(id+"F0.wireOp",EDGE,"E61"),sQuery(id+"F0.wireOp",EDGE,"E62"),sQuery(id+"F0.wireOp",EDGE,"E63"),sQuery(id+"F0.wireOp",EDGE,"E64"),sQuery(id+"F0.wireOp",EDGE,"E65"),sQuery(id+"F0.wireOp",EDGE,"E66"),sQuery(id+"F0.wireOp",EDGE,"E67"),sQuery(id+"F0.wireOp",EDGE,"E72"),sQuery(id+"F0.wireOp",EDGE,"E73"),sQuery(id+"F0.wireOp",EDGE,"E74"),sQuery(id+"F0.wireOp",EDGE,"E75")])],"isStart":false});
            var sketch = newSketch(context, id + "F14", { "sketchPlane" : qUnion([Q0])});
            skArc(sketch, "E149", {"start": v(-14.88, 394.6) * mm, "mid": v(35.12, 444.6) * mm, "end": v(-14.88, 494.6) * mm});
            skArc(sketch, "E150", {"start": v(-14.88, 494.6) * mm, "mid": v(35.12, 544.6) * mm, "end": v(-14.88, 594.6) * mm});
            skLineSegment(sketch, "E151", {"start": v(-14.88, 594.6) * mm, "end": v(-14.88, 394.6) * mm});
            skLineSegment(sketch, "E152", {"start": v(34.87, 549.6) * mm, "end": v(104.87, 549.6) * mm});
            skLineSegment(sketch, "E153", {"start": v(104.87, 549.6) * mm, "end": v(104.87, 539.6) * mm});
            skLineSegment(sketch, "E154", {"start": v(104.87, 539.6) * mm, "end": v(34.87, 539.6) * mm});
            skLineSegment(sketch, "E155", {"start": v(34.87, 449.6) * mm, "end": v(104.87, 449.6) * mm});
            skLineSegment(sketch, "E156", {"start": v(104.87, 449.6) * mm, "end": v(104.87, 439.6) * mm});
            skLineSegment(sketch, "E157", {"start": v(104.87, 439.6) * mm, "end": v(34.87, 439.6) * mm});
            skLineSegment(sketch, "E158", {"start": v(-14.88, -85.4) * mm, "end": v(361.58, -85.4) * mm, "construction": true});
            skLineSegment(sketch, "E159.MirrorCS", {"start": v(104.87, -620.4) * mm, "end": v(104.87, -610.4) * mm});
            skLineSegment(sketch, "E160.MirrorCS", {"start": v(104.87, -720.4) * mm, "end": v(104.87, -710.4) * mm});
            skLineSegment(sketch, "E161.MirrorCS", {"start": v(34.87, -620.4) * mm, "end": v(104.87, -620.4) * mm});
            skLineSegment(sketch, "E162.MirrorCS", {"start": v(104.87, -610.4) * mm, "end": v(34.87, -610.4) * mm});
            skArc(sketch, "E163.MirrorCS", {"start": v(-14.88, -565.4) * mm, "mid": v(35.12, -615.4) * mm, "end": v(-14.88, -665.4) * mm});
            skArc(sketch, "E164.MirrorCS", {"start": v(-14.88, -665.4) * mm, "mid": v(35.12, -715.4) * mm, "end": v(-14.88, -765.4) * mm});
            skLineSegment(sketch, "E165.MirrorCS", {"start": v(-14.88, -765.4) * mm, "end": v(-14.88, -565.4) * mm});
            skLineSegment(sketch, "E166.MirrorCS", {"start": v(34.87, -720.4) * mm, "end": v(104.87, -720.4) * mm});
            skLineSegment(sketch, "E167.MirrorCS", {"start": v(104.87, -710.4) * mm, "end": v(34.87, -710.4) * mm});
            skArc(sketch, "E168", {"start": v(-14.88, 604.6) * mm, "mid": v(35.12, 654.6) * mm, "end": v(-14.88, 704.6) * mm});
            skLineSegment(sketch, "E169", {"start": v(-14.88, 704.6) * mm, "end": v(-14.88, 604.6) * mm});
            skLineSegment(sketch, "E170", {"start": v(34.87, 659.6) * mm, "end": v(104.87, 659.6) * mm});
            skLineSegment(sketch, "E171", {"start": v(104.87, 659.6) * mm, "end": v(104.87, 649.6) * mm});
            skLineSegment(sketch, "E172", {"start": v(104.87, 649.6) * mm, "end": v(34.87, 649.6) * mm});
            skLineSegment(sketch, "E173.bottom", {"start": v(-14.88, -35.4) * mm, "end": v(85.12, -35.4) * mm});
            skLineSegment(sketch, "E173.top", {"start": v(-14.88, -135.4) * mm, "end": v(85.12, -135.4) * mm});
            skLineSegment(sketch, "E173.left", {"start": v(-14.88, -35.4) * mm, "end": v(-14.88, -135.4) * mm});
            skLineSegment(sketch, "E173.right", {"start": v(85.12, -35.4) * mm, "end": v(85.12, -135.4) * mm});
            skLineSegment(sketch, "E174", {"start": v(35.12, -35.4) * mm, "end": v(35.12, -135.4) * mm, "construction": true});
            skLineSegment(sketch, "E175", {"start": v(-14.88, -35.4) * mm, "end": v(85.12, -135.4) * mm});
            skLineSegment(sketch, "E176", {"start": v(-14.88, -135.4) * mm, "end": v(85.12, -35.4) * mm});
            skLineSegment(sketch, "E177.0.left", {"start": v(-14.88, -131.87) * mm, "end": v(81.58, -35.4) * mm});
            skLineSegment(sketch, "E177.0.right", {"start": v(-11.35, -135.4) * mm, "end": v(85.12, -38.94) * mm});
            skLineSegment(sketch, "E177.1.left", {"start": v(-11.35, -35.4) * mm, "end": v(85.12, -131.87) * mm});
            skLineSegment(sketch, "E177.1.right", {"start": v(-14.88, -38.94) * mm, "end": v(81.58, -135.4) * mm});
            skSolve(sketch);
        }
        {
            var Q0;
            {var subQ0=sQuery(id+"F14.wireOp",EDGE,"E169");Q0=makeQuery(id+"F14.imprint","IMPRINT",FACE,{"disambiguationData":[TD([[makeQuery(id+"F14.imprint","IMPRINT",EDGE,{"derivedFrom":subQ0}),-1.0]])]});}
            var Q1;
            {var subQ1=sQuery(id+"F14.wireOp",EDGE,"E150");var subQ4=makeQuery(id+"F14.imprint","INTERSECT",VERTEX,{"derivedFrom":[subQ1,sQuery(id+"F14.wireOp",EDGE,"E152")]});Q1=makeQuery(id+"F14.imprint","IMPRINT",FACE,{"disambiguationData":[TD([[makeQuery(id+"F14.imprint","IMPRINT",EDGE,{"disambiguationData":[TD([[subQ4,1.0]])],"derivedFrom":subQ1}),1.0]])]});}
            var Q2;
            {var subQ1=sQuery(id+"F14.wireOp",EDGE,"E149");var subQ4=makeQuery(id+"F14.imprint","INTERSECT",VERTEX,{"derivedFrom":[subQ1,sQuery(id+"F14.wireOp",EDGE,"E155")]});Q2=makeQuery(id+"F14.imprint","IMPRINT",FACE,{"disambiguationData":[TD([[makeQuery(id+"F14.imprint","IMPRINT",EDGE,{"disambiguationData":[TD([[subQ4,1.0]])],"derivedFrom":subQ1}),1.0]])]});}
            var Q3;
            {var subQ0=sQuery(id+"F14.wireOp",EDGE,"E163.MirrorCS");var subQ4=makeQuery(id+"F14.imprint","INTERSECT",VERTEX,{"derivedFrom":[sQuery(id+"F14.wireOp",EDGE,"E161.MirrorCS"),subQ0]});Q3=makeQuery(id+"F14.imprint","IMPRINT",FACE,{"disambiguationData":[TD([[makeQuery(id+"F14.imprint","IMPRINT",EDGE,{"disambiguationData":[TD([[subQ4,1.0]])],"derivedFrom":subQ0}),-1.0]])]});}
            var Q4;
            {var subQ1=sQuery(id+"F14.wireOp",EDGE,"E164.MirrorCS");var subQ4=makeQuery(id+"F14.imprint","INTERSECT",VERTEX,{"derivedFrom":[subQ1,sQuery(id+"F14.wireOp",EDGE,"E166.MirrorCS")]});Q4=makeQuery(id+"F14.imprint","IMPRINT",FACE,{"disambiguationData":[TD([[makeQuery(id+"F14.imprint","IMPRINT",EDGE,{"disambiguationData":[TD([[subQ4,1.0]])],"derivedFrom":subQ1}),-1.0]])]});}
            extrude(context, id + "F15", {"entities" : qUnion([Q0, Q1, Q2, Q3, Q4]), "depth" : 25 * mm});
        }
        {
            var Q0;
            Q0=makeQuery(id+"F14.imprint","IMPRINT",FACE,{"disambiguationData":[TD([[makeQuery(id+"F14.imprint","IMPRINT",EDGE,{"derivedFrom":sQuery(id+"F14.wireOp",EDGE,"E160.MirrorCS")}),1.0]])]});
            var Q1;
            Q1=makeQuery(id+"F14.imprint","IMPRINT",FACE,{"disambiguationData":[TD([[makeQuery(id+"F14.imprint","IMPRINT",EDGE,{"derivedFrom":sQuery(id+"F14.wireOp",EDGE,"E159.MirrorCS")}),1.0]])]});
            var Q2;
            {var subQ0=sQuery(id+"F14.wireOp",EDGE,"E155");Q2=makeQuery(id+"F14.imprint","IMPRINT",FACE,{"disambiguationData":[TD([[makeQuery(id+"F14.imprint","IMPRINT",EDGE,{"derivedFrom":subQ0}),-1.0]])]});}
            var Q3;
            {var subQ0=sQuery(id+"F14.wireOp",EDGE,"E152");Q3=makeQuery(id+"F14.imprint","IMPRINT",FACE,{"disambiguationData":[TD([[makeQuery(id+"F14.imprint","IMPRINT",EDGE,{"derivedFrom":subQ0}),-1.0]])]});}
            var Q4;
            {var subQ0=sQuery(id+"F14.wireOp",EDGE,"E170");Q4=makeQuery(id+"F14.imprint","IMPRINT",FACE,{"disambiguationData":[TD([[makeQuery(id+"F14.imprint","IMPRINT",EDGE,{"derivedFrom":subQ0}),-1.0]])]});}
            extrude(context, id + "F16", {"entities" : qUnion([Q0, Q1, Q2, Q3, Q4]), "depth" : 24 * mm});
        }
        {
            var Q0;
            {var subQ0=sQuery(id+"F14.wireOp",EDGE,"E177.0.left");var subQ1=sQuery(id+"F14.wireOp",EDGE,"E173.left");var subQ2=makeQuery(id+"F14.imprint","INTERSECT",VERTEX,{"derivedFrom":[subQ1,subQ0]});Q0=makeQuery(id+"F14.imprint","IMPRINT",FACE,{"disambiguationData":[TD([[makeQuery(id+"F14.imprint","IMPRINT",EDGE,{"disambiguationData":[TD([[subQ2,-1.0]])],"derivedFrom":subQ1}),-1.0]])]});}
            var Q1;
            {var subQ0=sQuery(id+"F14.wireOp",EDGE,"E177.0.left");var subQ1=sQuery(id+"F14.wireOp",EDGE,"E173.bottom");var subQ2=makeQuery(id+"F14.imprint","INTERSECT",VERTEX,{"derivedFrom":[subQ1,subQ0]});Q1=makeQuery(id+"F14.imprint","IMPRINT",FACE,{"disambiguationData":[TD([[makeQuery(id+"F14.imprint","IMPRINT",EDGE,{"disambiguationData":[TD([[subQ2,1.0]])],"derivedFrom":subQ1}),-1.0]])]});}
            var Q2;
            {var subQ0=sQuery(id+"F14.wireOp",EDGE,"E177.0.right");var subQ1=sQuery(id+"F14.wireOp",EDGE,"E173.right");var subQ2=makeQuery(id+"F14.imprint","INTERSECT",VERTEX,{"derivedFrom":[subQ1,subQ0]});Q2=makeQuery(id+"F14.imprint","IMPRINT",FACE,{"disambiguationData":[TD([[makeQuery(id+"F14.imprint","IMPRINT",EDGE,{"disambiguationData":[TD([[subQ2,-1.0]])],"derivedFrom":subQ1}),-1.0]])]});}
            var Q3;
            {var subQ0=sQuery(id+"F14.wireOp",EDGE,"E177.0.right");var subQ1=sQuery(id+"F14.wireOp",EDGE,"E173.top");var subQ2=makeQuery(id+"F14.imprint","INTERSECT",VERTEX,{"derivedFrom":[subQ1,subQ0]});Q3=makeQuery(id+"F14.imprint","IMPRINT",FACE,{"disambiguationData":[TD([[makeQuery(id+"F14.imprint","IMPRINT",EDGE,{"disambiguationData":[TD([[subQ2,-1.0]])],"derivedFrom":subQ1}),1.0]])]});}
            extrude(context, id + "F17", {"entities" : qUnion([Q0, Q1, Q2, Q3]), "depth" : 25 * mm});
        }
        {
            var Q0;
            {var subQ1=sQuery(id+"F14.wireOp",EDGE,"E173.top");var subQ3=sQuery(id+"F14.wireOp",EDGE,"E177.0.right");var subQ4=makeQuery(id+"F14.imprint","INTERSECT",VERTEX,{"derivedFrom":[subQ1,subQ3]});Q0=makeQuery(id+"F14.imprint","IMPRINT",FACE,{"disambiguationData":[TD([[makeQuery(id+"F14.imprint","IMPRINT",EDGE,{"disambiguationData":[TD([[subQ4,-1.0]])],"derivedFrom":subQ3}),1.0]])]});}
            var Q1;
            {var subQ1=sQuery(id+"F14.wireOp",EDGE,"E173.left");var subQ3=sQuery(id+"F14.wireOp",EDGE,"E177.0.left");var subQ4=makeQuery(id+"F14.imprint","INTERSECT",VERTEX,{"derivedFrom":[subQ1,subQ3]});Q1=makeQuery(id+"F14.imprint","IMPRINT",FACE,{"disambiguationData":[TD([[makeQuery(id+"F14.imprint","IMPRINT",EDGE,{"disambiguationData":[TD([[subQ4,-1.0]])],"derivedFrom":subQ3}),-1.0]])]});}
            var Q2;
            {var subQ0=sQuery(id+"F14.wireOp",EDGE,"E175");var subQ5=sQuery(id+"F14.wireOp",EDGE,"E177.0.right");var subQ6=makeQuery(id+"F14.imprint","INTERSECT",VERTEX,{"derivedFrom":[subQ0,subQ5]});Q2=makeQuery(id+"F14.imprint","IMPRINT",FACE,{"disambiguationData":[TD([[makeQuery(id+"F14.imprint","IMPRINT",EDGE,{"disambiguationData":[TD([[subQ6,1.0]])],"derivedFrom":subQ5}),-1.0]])]});}
            var Q3;
            {var subQ0=sQuery(id+"F14.wireOp",EDGE,"E175");var subQ5=sQuery(id+"F14.wireOp",EDGE,"E177.0.right");var subQ6=makeQuery(id+"F14.imprint","INTERSECT",VERTEX,{"derivedFrom":[subQ0,subQ5]});Q3=makeQuery(id+"F14.imprint","IMPRINT",FACE,{"disambiguationData":[TD([[makeQuery(id+"F14.imprint","IMPRINT",EDGE,{"disambiguationData":[TD([[subQ6,-1.0]])],"derivedFrom":subQ5}),-1.0]])]});}
            var Q4;
            {var subQ0=sQuery(id+"F14.wireOp",EDGE,"E176");var subQ1=sQuery(id+"F14.wireOp",EDGE,"E175");var subQ2=makeQuery(id+"F14.imprint","INTERSECT",VERTEX,{"derivedFrom":[subQ1,subQ0]});Q4=makeQuery(id+"F14.imprint","IMPRINT",FACE,{"disambiguationData":[TD([[makeQuery(id+"F14.imprint","IMPRINT",EDGE,{"disambiguationData":[TD([[subQ2,-1.0]])],"derivedFrom":subQ1}),1.0]])]});}
            var Q5;
            {var subQ1=sQuery(id+"F14.wireOp",EDGE,"E173.bottom");var subQ3=sQuery(id+"F14.wireOp",EDGE,"E177.0.left");var subQ4=makeQuery(id+"F14.imprint","INTERSECT",VERTEX,{"derivedFrom":[subQ1,subQ3]});Q5=makeQuery(id+"F14.imprint","IMPRINT",FACE,{"disambiguationData":[TD([[makeQuery(id+"F14.imprint","IMPRINT",EDGE,{"disambiguationData":[TD([[subQ4,1.0]])],"derivedFrom":subQ3}),-1.0]])]});}
            var Q6;
            {var subQ1=sQuery(id+"F14.wireOp",EDGE,"E173.right");var subQ3=sQuery(id+"F14.wireOp",EDGE,"E177.0.right");var subQ4=makeQuery(id+"F14.imprint","INTERSECT",VERTEX,{"derivedFrom":[subQ1,subQ3]});Q6=makeQuery(id+"F14.imprint","IMPRINT",FACE,{"disambiguationData":[TD([[makeQuery(id+"F14.imprint","IMPRINT",EDGE,{"disambiguationData":[TD([[subQ4,1.0]])],"derivedFrom":subQ3}),1.0]])]});}
            var Q7;
            {var subQ0=sQuery(id+"F14.wireOp",EDGE,"E175");var subQ5=sQuery(id+"F14.wireOp",EDGE,"E177.0.left");var subQ6=makeQuery(id+"F14.imprint","INTERSECT",VERTEX,{"derivedFrom":[subQ0,subQ5]});Q7=makeQuery(id+"F14.imprint","IMPRINT",FACE,{"disambiguationData":[TD([[makeQuery(id+"F14.imprint","IMPRINT",EDGE,{"disambiguationData":[TD([[subQ6,-1.0]])],"derivedFrom":subQ5}),1.0]])]});}
            var Q8;
            {var subQ0=sQuery(id+"F14.wireOp",EDGE,"E175");var subQ5=sQuery(id+"F14.wireOp",EDGE,"E177.0.left");var subQ6=makeQuery(id+"F14.imprint","INTERSECT",VERTEX,{"derivedFrom":[subQ0,subQ5]});Q8=makeQuery(id+"F14.imprint","IMPRINT",FACE,{"disambiguationData":[TD([[makeQuery(id+"F14.imprint","IMPRINT",EDGE,{"disambiguationData":[TD([[subQ6,1.0]])],"derivedFrom":subQ5}),1.0]])]});}
            var Q9;
            {var subQ0=sQuery(id+"F14.wireOp",EDGE,"E177.0.left");var subQ1=sQuery(id+"F14.wireOp",EDGE,"E175");var subQ2=makeQuery(id+"F14.imprint","INTERSECT",VERTEX,{"derivedFrom":[subQ1,subQ0]});Q9=makeQuery(id+"F14.imprint","IMPRINT",FACE,{"disambiguationData":[TD([[makeQuery(id+"F14.imprint","IMPRINT",EDGE,{"disambiguationData":[TD([[subQ2,-1.0]])],"derivedFrom":subQ1}),-1.0]])]});}
            var Q10;
            {var subQ0=sQuery(id+"F14.wireOp",EDGE,"E177.0.left");var subQ1=sQuery(id+"F14.wireOp",EDGE,"E175");var subQ2=makeQuery(id+"F14.imprint","INTERSECT",VERTEX,{"derivedFrom":[subQ1,subQ0]});Q10=makeQuery(id+"F14.imprint","IMPRINT",FACE,{"disambiguationData":[TD([[makeQuery(id+"F14.imprint","IMPRINT",EDGE,{"disambiguationData":[TD([[subQ2,-1.0]])],"derivedFrom":subQ1}),1.0]])]});}
            var Q11;
            {var subQ0=sQuery(id+"F14.wireOp",EDGE,"E176");var subQ1=sQuery(id+"F14.wireOp",EDGE,"E175");var subQ2=makeQuery(id+"F14.imprint","INTERSECT",VERTEX,{"derivedFrom":[subQ1,subQ0]});Q11=makeQuery(id+"F14.imprint","IMPRINT",FACE,{"disambiguationData":[TD([[makeQuery(id+"F14.imprint","IMPRINT",EDGE,{"disambiguationData":[TD([[subQ2,-1.0]])],"derivedFrom":subQ1}),-1.0]])]});}
            extrude(context, id + "F18", {"entities" : qUnion([Q0, Q1, Q2, Q3, Q4, Q5, Q6, Q7, Q8, Q9, Q10, Q11]), "operationType" : NewBodyOperationType.ADD, "depth" : 24 * mm});
        }
        {
            var Q0;
            Q0=makeQuery(id+"F1.opExtrude","CAP_FACE",FACE,{"disambiguationData":[OSD([sQuery(id+"F0.wireOp",EDGE,"E0"),sQuery(id+"F0.wireOp",EDGE,"E1"),sQuery(id+"F0.wireOp",EDGE,"E2"),sQuery(id+"F0.wireOp",EDGE,"E3"),sQuery(id+"F0.wireOp",EDGE,"E4"),sQuery(id+"F0.wireOp",EDGE,"E5"),sQuery(id+"F0.wireOp",EDGE,"E6"),sQuery(id+"F0.wireOp",EDGE,"E7"),sQuery(id+"F0.wireOp",EDGE,"E8"),sQuery(id+"F0.wireOp",EDGE,"E9"),sQuery(id+"F0.wireOp",EDGE,"E10"),sQuery(id+"F0.wireOp",EDGE,"E11"),sQuery(id+"F0.wireOp",EDGE,"E12"),sQuery(id+"F0.wireOp",EDGE,"E13"),sQuery(id+"F0.wireOp",EDGE,"E14"),sQuery(id+"F0.wireOp",EDGE,"E15"),sQuery(id+"F0.wireOp",EDGE,"E16"),sQuery(id+"F0.wireOp",EDGE,"E17"),sQuery(id+"F0.wireOp",EDGE,"E18"),sQuery(id+"F0.wireOp",EDGE,"E19"),sQuery(id+"F0.wireOp",EDGE,"E20"),sQuery(id+"F0.wireOp",EDGE,"E21"),sQuery(id+"F0.wireOp",EDGE,"E22"),sQuery(id+"F0.wireOp",EDGE,"E23"),sQuery(id+"F0.wireOp",EDGE,"E44"),sQuery(id+"F0.wireOp",EDGE,"E45"),sQuery(id+"F0.wireOp",EDGE,"E46"),sQuery(id+"F0.wireOp",EDGE,"E47"),sQuery(id+"F0.wireOp",EDGE,"E48"),sQuery(id+"F0.wireOp",EDGE,"E49"),sQuery(id+"F0.wireOp",EDGE,"E50"),sQuery(id+"F0.wireOp",EDGE,"E51"),sQuery(id+"F0.wireOp",EDGE,"E52"),sQuery(id+"F0.wireOp",EDGE,"E53"),sQuery(id+"F0.wireOp",EDGE,"E54"),sQuery(id+"F0.wireOp",EDGE,"E55"),sQuery(id+"F0.wireOp",EDGE,"E56"),sQuery(id+"F0.wireOp",EDGE,"E57"),sQuery(id+"F0.wireOp",EDGE,"E58"),sQuery(id+"F0.wireOp",EDGE,"E59"),sQuery(id+"F0.wireOp",EDGE,"E60"),sQuery(id+"F0.wireOp",EDGE,"E61"),sQuery(id+"F0.wireOp",EDGE,"E62"),sQuery(id+"F0.wireOp",EDGE,"E63"),sQuery(id+"F0.wireOp",EDGE,"E64"),sQuery(id+"F0.wireOp",EDGE,"E65"),sQuery(id+"F0.wireOp",EDGE,"E66"),sQuery(id+"F0.wireOp",EDGE,"E67"),sQuery(id+"F0.wireOp",EDGE,"E72"),sQuery(id+"F0.wireOp",EDGE,"E73"),sQuery(id+"F0.wireOp",EDGE,"E74"),sQuery(id+"F0.wireOp",EDGE,"E75")])],"isStart":false});
            var sketch = newSketch(context, id + "F19", { "sketchPlane" : qUnion([Q0])});
            skLineSegment(sketch, "E178", {"start": v(-4269.88, 554.6) * mm, "end": v(-3893.42, 554.6) * mm, "construction": true});
            skLineSegment(sketch, "E179.bottom", {"start": v(-4269.88, 604.6) * mm, "end": v(-4169.88, 604.6) * mm});
            skLineSegment(sketch, "E179.top", {"start": v(-4269.88, 504.6) * mm, "end": v(-4169.88, 504.6) * mm});
            skLineSegment(sketch, "E179.left", {"start": v(-4269.88, 604.6) * mm, "end": v(-4269.88, 504.6) * mm});
            skLineSegment(sketch, "E179.right", {"start": v(-4169.88, 604.6) * mm, "end": v(-4169.88, 504.6) * mm});
            skLineSegment(sketch, "E180", {"start": v(-4219.88, 604.6) * mm, "end": v(-4219.88, 504.6) * mm, "construction": true});
            skLineSegment(sketch, "E181", {"start": v(-4269.88, 604.6) * mm, "end": v(-4169.88, 504.6) * mm});
            skLineSegment(sketch, "E182", {"start": v(-4269.88, 504.6) * mm, "end": v(-4169.88, 604.6) * mm});
            skSolve(sketch);
        }
        {
            var Q0;
            {var subQ0=sQuery(id+"F19.wireOp",EDGE,"E179.bottom");Q0=makeQuery(id+"F19.imprint","IMPRINT",FACE,{"disambiguationData":[TD([[makeQuery(id+"F19.imprint","IMPRINT",EDGE,{"derivedFrom":subQ0}),-1.0]])]});}
            var Q1;
            {var subQ0=sQuery(id+"F19.wireOp",EDGE,"E179.top");Q1=makeQuery(id+"F19.imprint","IMPRINT",FACE,{"disambiguationData":[TD([[makeQuery(id+"F19.imprint","IMPRINT",EDGE,{"derivedFrom":subQ0}),1.0]])]});}
            extrude(context, id + "F20", {"entities" : qUnion([Q0, Q1]), "depth" : 25 * mm});
        }
        {
            var Q0;
            {var subQ0=sQuery(id+"F19.wireOp",EDGE,"E179.left");Q0=makeQuery(id+"F19.imprint","IMPRINT",FACE,{"disambiguationData":[TD([[makeQuery(id+"F19.imprint","IMPRINT",EDGE,{"derivedFrom":subQ0}),-1.0]])]});}
            var Q1;
            {var subQ0=sQuery(id+"F19.wireOp",EDGE,"E179.right");Q1=makeQuery(id+"F19.imprint","IMPRINT",FACE,{"disambiguationData":[TD([[makeQuery(id+"F19.imprint","IMPRINT",EDGE,{"derivedFrom":subQ0}),-1.0]])]});}
            extrude(context, id + "F21", {"entities" : qUnion([Q0, Q1]), "depth" : 24 * mm});
        }
        {
            var Q0;
            Q0=makeQuery(id+"F1.opExtrude","CAP_FACE",FACE,{"disambiguationData":[OSD([sQuery(id+"F0.wireOp",EDGE,"E0"),sQuery(id+"F0.wireOp",EDGE,"E1"),sQuery(id+"F0.wireOp",EDGE,"E2"),sQuery(id+"F0.wireOp",EDGE,"E3"),sQuery(id+"F0.wireOp",EDGE,"E4"),sQuery(id+"F0.wireOp",EDGE,"E5"),sQuery(id+"F0.wireOp",EDGE,"E6"),sQuery(id+"F0.wireOp",EDGE,"E7"),sQuery(id+"F0.wireOp",EDGE,"E8"),sQuery(id+"F0.wireOp",EDGE,"E9"),sQuery(id+"F0.wireOp",EDGE,"E10"),sQuery(id+"F0.wireOp",EDGE,"E11"),sQuery(id+"F0.wireOp",EDGE,"E12"),sQuery(id+"F0.wireOp",EDGE,"E13"),sQuery(id+"F0.wireOp",EDGE,"E14"),sQuery(id+"F0.wireOp",EDGE,"E15"),sQuery(id+"F0.wireOp",EDGE,"E16"),sQuery(id+"F0.wireOp",EDGE,"E17"),sQuery(id+"F0.wireOp",EDGE,"E18"),sQuery(id+"F0.wireOp",EDGE,"E19"),sQuery(id+"F0.wireOp",EDGE,"E20"),sQuery(id+"F0.wireOp",EDGE,"E21"),sQuery(id+"F0.wireOp",EDGE,"E22"),sQuery(id+"F0.wireOp",EDGE,"E23"),sQuery(id+"F0.wireOp",EDGE,"E44"),sQuery(id+"F0.wireOp",EDGE,"E45"),sQuery(id+"F0.wireOp",EDGE,"E46"),sQuery(id+"F0.wireOp",EDGE,"E47"),sQuery(id+"F0.wireOp",EDGE,"E48"),sQuery(id+"F0.wireOp",EDGE,"E49"),sQuery(id+"F0.wireOp",EDGE,"E50"),sQuery(id+"F0.wireOp",EDGE,"E51"),sQuery(id+"F0.wireOp",EDGE,"E52"),sQuery(id+"F0.wireOp",EDGE,"E53"),sQuery(id+"F0.wireOp",EDGE,"E54"),sQuery(id+"F0.wireOp",EDGE,"E55"),sQuery(id+"F0.wireOp",EDGE,"E56"),sQuery(id+"F0.wireOp",EDGE,"E57"),sQuery(id+"F0.wireOp",EDGE,"E58"),sQuery(id+"F0.wireOp",EDGE,"E59"),sQuery(id+"F0.wireOp",EDGE,"E60"),sQuery(id+"F0.wireOp",EDGE,"E61"),sQuery(id+"F0.wireOp",EDGE,"E62"),sQuery(id+"F0.wireOp",EDGE,"E63"),sQuery(id+"F0.wireOp",EDGE,"E64"),sQuery(id+"F0.wireOp",EDGE,"E65"),sQuery(id+"F0.wireOp",EDGE,"E66"),sQuery(id+"F0.wireOp",EDGE,"E67"),sQuery(id+"F0.wireOp",EDGE,"E72"),sQuery(id+"F0.wireOp",EDGE,"E73"),sQuery(id+"F0.wireOp",EDGE,"E74"),sQuery(id+"F0.wireOp",EDGE,"E75")])],"isStart":false});
            var sketch = newSketch(context, id + "F22", { "sketchPlane" : qUnion([Q0])});
            skLineSegment(sketch, "E183", {"start": v(6851.12, 1604.6) * mm, "end": v(7227.58, 1604.6) * mm, "construction": true});
            skLineSegment(sketch, "E184.bottom", {"start": v(6851.12, 1654.6) * mm, "end": v(6951.12, 1654.6) * mm});
            skLineSegment(sketch, "E184.top", {"start": v(6851.12, 1554.6) * mm, "end": v(6951.12, 1554.6) * mm});
            skLineSegment(sketch, "E184.left", {"start": v(6851.12, 1654.6) * mm, "end": v(6851.12, 1554.6) * mm});
            skLineSegment(sketch, "E184.right", {"start": v(6951.12, 1654.6) * mm, "end": v(6951.12, 1554.6) * mm});
            skLineSegment(sketch, "E185", {"start": v(6901.12, 1654.6) * mm, "end": v(6901.12, 1554.6) * mm, "construction": true});
            skLineSegment(sketch, "E186", {"start": v(6851.12, 1654.6) * mm, "end": v(6951.12, 1554.6) * mm});
            skLineSegment(sketch, "E187", {"start": v(6851.12, 1554.6) * mm, "end": v(6951.12, 1654.6) * mm});
            skSolve(sketch);
        }
        {
            var Q0;
            {var subQ0=sQuery(id+"F22.wireOp",EDGE,"E184.left");Q0=makeQuery(id+"F22.imprint","IMPRINT",FACE,{"disambiguationData":[TD([[makeQuery(id+"F22.imprint","IMPRINT",EDGE,{"derivedFrom":subQ0}),1.0]])]});}
            var Q1;
            {var subQ0=sQuery(id+"F22.wireOp",EDGE,"E184.right");Q1=makeQuery(id+"F22.imprint","IMPRINT",FACE,{"disambiguationData":[TD([[makeQuery(id+"F22.imprint","IMPRINT",EDGE,{"derivedFrom":subQ0}),-1.0]])]});}
            extrude(context, id + "F23", {"entities" : qUnion([Q0, Q1]), "depth" : 25 * mm});
        }
        {
            var Q0;
            {var subQ0=sQuery(id+"F22.wireOp",EDGE,"E184.bottom");Q0=makeQuery(id+"F22.imprint","IMPRINT",FACE,{"disambiguationData":[TD([[makeQuery(id+"F22.imprint","IMPRINT",EDGE,{"derivedFrom":subQ0}),1.0]])]});}
            var Q1;
            {var subQ0=sQuery(id+"F22.wireOp",EDGE,"E184.top");Q1=makeQuery(id+"F22.imprint","IMPRINT",FACE,{"disambiguationData":[TD([[makeQuery(id+"F22.imprint","IMPRINT",EDGE,{"derivedFrom":subQ0}),1.0]])]});}
            extrude(context, id + "F24", {"entities" : qUnion([Q0, Q1]), "depth" : 25 * mm});
        }
        {
            var Q0;
            Q0=makeQuery(id+"F1.opExtrude","CAP_FACE",FACE,{"disambiguationData":[OSD([sQuery(id+"F0.wireOp",EDGE,"E0"),sQuery(id+"F0.wireOp",EDGE,"E1"),sQuery(id+"F0.wireOp",EDGE,"E2"),sQuery(id+"F0.wireOp",EDGE,"E3"),sQuery(id+"F0.wireOp",EDGE,"E4"),sQuery(id+"F0.wireOp",EDGE,"E5"),sQuery(id+"F0.wireOp",EDGE,"E6"),sQuery(id+"F0.wireOp",EDGE,"E7"),sQuery(id+"F0.wireOp",EDGE,"E8"),sQuery(id+"F0.wireOp",EDGE,"E9"),sQuery(id+"F0.wireOp",EDGE,"E10"),sQuery(id+"F0.wireOp",EDGE,"E11"),sQuery(id+"F0.wireOp",EDGE,"E12"),sQuery(id+"F0.wireOp",EDGE,"E13"),sQuery(id+"F0.wireOp",EDGE,"E14"),sQuery(id+"F0.wireOp",EDGE,"E15"),sQuery(id+"F0.wireOp",EDGE,"E16"),sQuery(id+"F0.wireOp",EDGE,"E17"),sQuery(id+"F0.wireOp",EDGE,"E18"),sQuery(id+"F0.wireOp",EDGE,"E19"),sQuery(id+"F0.wireOp",EDGE,"E20"),sQuery(id+"F0.wireOp",EDGE,"E21"),sQuery(id+"F0.wireOp",EDGE,"E22"),sQuery(id+"F0.wireOp",EDGE,"E23"),sQuery(id+"F0.wireOp",EDGE,"E44"),sQuery(id+"F0.wireOp",EDGE,"E45"),sQuery(id+"F0.wireOp",EDGE,"E46"),sQuery(id+"F0.wireOp",EDGE,"E47"),sQuery(id+"F0.wireOp",EDGE,"E48"),sQuery(id+"F0.wireOp",EDGE,"E49"),sQuery(id+"F0.wireOp",EDGE,"E50"),sQuery(id+"F0.wireOp",EDGE,"E51"),sQuery(id+"F0.wireOp",EDGE,"E52"),sQuery(id+"F0.wireOp",EDGE,"E53"),sQuery(id+"F0.wireOp",EDGE,"E54"),sQuery(id+"F0.wireOp",EDGE,"E55"),sQuery(id+"F0.wireOp",EDGE,"E56"),sQuery(id+"F0.wireOp",EDGE,"E57"),sQuery(id+"F0.wireOp",EDGE,"E58"),sQuery(id+"F0.wireOp",EDGE,"E59"),sQuery(id+"F0.wireOp",EDGE,"E60"),sQuery(id+"F0.wireOp",EDGE,"E61"),sQuery(id+"F0.wireOp",EDGE,"E62"),sQuery(id+"F0.wireOp",EDGE,"E63"),sQuery(id+"F0.wireOp",EDGE,"E64"),sQuery(id+"F0.wireOp",EDGE,"E65"),sQuery(id+"F0.wireOp",EDGE,"E66"),sQuery(id+"F0.wireOp",EDGE,"E67"),sQuery(id+"F0.wireOp",EDGE,"E72"),sQuery(id+"F0.wireOp",EDGE,"E73"),sQuery(id+"F0.wireOp",EDGE,"E74"),sQuery(id+"F0.wireOp",EDGE,"E75")])],"isStart":false});
            var sketch = newSketch(context, id + "F25", { "sketchPlane" : qUnion([Q0])});
            skArc(sketch, "E188", {"start": v(-3819.88, 1654.6) * mm, "mid": v(-3769.88, 1604.6) * mm, "end": v(-3719.88, 1654.6) * mm});
            skLineSegment(sketch, "E189", {"start": v(-3819.88, 1654.6) * mm, "end": v(-3719.88, 1654.6) * mm});
            skLineSegment(sketch, "E190", {"start": v(-3774.88, 1604.85) * mm, "end": v(-3774.88, 1534.85) * mm});
            skLineSegment(sketch, "E191", {"start": v(-3774.88, 1534.85) * mm, "end": v(-3764.88, 1534.85) * mm});
            skLineSegment(sketch, "E192", {"start": v(-3764.88, 1534.85) * mm, "end": v(-3764.88, 1604.85) * mm});
            skLineSegment(sketch, "E193", {"start": v(-791.38, 1654.6) * mm, "end": v(-791.38, 1365.37) * mm, "construction": true});
            skLineSegment(sketch, "E194.MirrorCS", {"start": v(2192.12, 1534.85) * mm, "end": v(2182.12, 1534.85) * mm});
            skLineSegment(sketch, "E195.MirrorCS", {"start": v(2192.12, 1604.85) * mm, "end": v(2192.12, 1534.85) * mm});
            skArc(sketch, "E196.MirrorCS", {"start": v(2237.12, 1654.6) * mm, "mid": v(2187.12, 1604.6) * mm, "end": v(2137.12, 1654.6) * mm});
            skLineSegment(sketch, "E197.MirrorCS", {"start": v(2182.12, 1534.85) * mm, "end": v(2182.12, 1604.85) * mm});
            skLineSegment(sketch, "E198.MirrorCS", {"start": v(2237.12, 1654.6) * mm, "end": v(2137.12, 1654.6) * mm});
            skLineSegment(sketch, "E199.MirrorCS", {"start": v(5997.12, 1534.6) * mm, "end": v(5987.12, 1534.6) * mm});
            skLineSegment(sketch, "E200.MirrorCS", {"start": v(5997.12, 1604.85) * mm, "end": v(5997.12, 1534.6) * mm});
            skArc(sketch, "E201.MirrorCS", {"start": v(6042.12, 1654.6) * mm, "mid": v(5992.12, 1604.6) * mm, "end": v(5942.12, 1654.6) * mm});
            skLineSegment(sketch, "E202.MirrorCS", {"start": v(5987.12, 1534.6) * mm, "end": v(5987.12, 1604.85) * mm});
            skLineSegment(sketch, "E203.MirrorCS", {"start": v(6042.12, 1654.6) * mm, "end": v(5942.12, 1654.6) * mm});
            skPoint(sketch, "E204.orphan", {"position": v(5997.12, 1604.6) * mm});
            skSolve(sketch);
        }
        {
            var Q0;
            {var subQ0=sQuery(id+"F25.wireOp",EDGE,"E189");Q0=makeQuery(id+"F25.imprint","IMPRINT",FACE,{"disambiguationData":[TD([[makeQuery(id+"F25.imprint","IMPRINT",EDGE,{"derivedFrom":subQ0}),-1.0]])]});}
            var Q1;
            {var subQ2=sQuery(id+"F25.wireOp",EDGE,"E198.MirrorCS");Q1=makeQuery(id+"F25.imprint","IMPRINT",FACE,{"disambiguationData":[TD([[makeQuery(id+"F25.imprint","IMPRINT",EDGE,{"derivedFrom":subQ2}),1.0]])]});}
            var Q2;
            Q2=makeQuery(id+"F25.imprint","IMPRINT",FACE,{"disambiguationData":[TD([[makeQuery(id+"F25.imprint","IMPRINT",EDGE,{"derivedFrom":sQuery(id+"F25.wireOp",EDGE,"E201.MirrorCS")}),-1.0]])]});
            extrude(context, id + "F26", {"entities" : qUnion([Q0, Q1, Q2]), "depth" : 25 * mm});
        }
        {
            var Q0;
            Q0=makeQuery(id+"F25.imprint","IMPRINT",FACE,{"disambiguationData":[TD([[makeQuery(id+"F25.imprint","IMPRINT",EDGE,{"derivedFrom":sQuery(id+"F25.wireOp",EDGE,"E199.MirrorCS")}),-1.0]])]});
            var Q1;
            Q1=makeQuery(id+"F25.imprint","IMPRINT",FACE,{"disambiguationData":[TD([[makeQuery(id+"F25.imprint","IMPRINT",EDGE,{"derivedFrom":sQuery(id+"F25.wireOp",EDGE,"E194.MirrorCS")}),-1.0]])]});
            var Q2;
            {var subQ0=sQuery(id+"F25.wireOp",EDGE,"E190");Q2=makeQuery(id+"F25.imprint","IMPRINT",FACE,{"disambiguationData":[TD([[makeQuery(id+"F25.imprint","IMPRINT",EDGE,{"derivedFrom":subQ0}),1.0]])]});}
            extrude(context, id + "F27", {"entities" : qUnion([Q0, Q1, Q2]), "depth" : 24 * mm});
        }
        {
            var Q0;
            Q0=makeQuery(id+"F1.opExtrude","CAP_FACE",FACE,{"disambiguationData":[OSD([sQuery(id+"F0.wireOp",EDGE,"E24"),sQuery(id+"F0.wireOp",EDGE,"E25"),sQuery(id+"F0.wireOp",EDGE,"E26"),sQuery(id+"F0.wireOp",EDGE,"E27"),sQuery(id+"F0.wireOp",EDGE,"E28"),sQuery(id+"F0.wireOp",EDGE,"E29"),sQuery(id+"F0.wireOp",EDGE,"E30"),sQuery(id+"F0.wireOp",EDGE,"E31"),sQuery(id+"F0.wireOp",EDGE,"E32"),sQuery(id+"F0.wireOp",EDGE,"E33"),sQuery(id+"F0.wireOp",EDGE,"E34"),sQuery(id+"F0.wireOp",EDGE,"E35"),sQuery(id+"F0.wireOp",EDGE,"E36"),sQuery(id+"F0.wireOp",EDGE,"E37"),sQuery(id+"F0.wireOp",EDGE,"E38"),sQuery(id+"F0.wireOp",EDGE,"E39"),sQuery(id+"F0.wireOp",EDGE,"E40"),sQuery(id+"F0.wireOp",EDGE,"E41"),sQuery(id+"F0.wireOp",EDGE,"E42"),sQuery(id+"F0.wireOp",EDGE,"E43"),sQuery(id+"F0.wireOp",EDGE,"E68"),sQuery(id+"F0.wireOp",EDGE,"E69"),sQuery(id+"F0.wireOp",EDGE,"E70"),sQuery(id+"F0.wireOp",EDGE,"E71")])],"isStart":false});
            var sketch = newSketch(context, id + "F28", { "sketchPlane" : qUnion([Q0])});
            skArc(sketch, "E205", {"start": v(2651.12, -2565.4) * mm, "mid": v(2601.12, -2515.4) * mm, "end": v(2551.12, -2565.4) * mm});
            skLineSegment(sketch, "E206", {"start": v(2551.12, -2565.4) * mm, "end": v(2651.12, -2565.4) * mm});
            skLineSegment(sketch, "E207", {"start": v(2596.12, -2515.65) * mm, "end": v(2596.12, -2445.65) * mm});
            skLineSegment(sketch, "E208", {"start": v(2596.12, -2445.65) * mm, "end": v(2606.12, -2445.65) * mm});
            skLineSegment(sketch, "E209", {"start": v(2606.12, -2445.65) * mm, "end": v(2606.12, -2515.65) * mm});
            skSolve(sketch);
        }
        {
            var Q0;
            {var subQ0=sQuery(id+"F28.wireOp",EDGE,"E206");Q0=makeQuery(id+"F28.imprint","IMPRINT",FACE,{"disambiguationData":[TD([[makeQuery(id+"F28.imprint","IMPRINT",EDGE,{"derivedFrom":subQ0}),-1.0]])]});}
            extrude(context, id + "F29", {"entities" : qUnion([Q0]), "depth" : 25 * mm});
        }
        {
            var Q0;
            {var subQ0=sQuery(id+"F28.wireOp",EDGE,"E207");Q0=makeQuery(id+"F28.imprint","IMPRINT",FACE,{"disambiguationData":[TD([[makeQuery(id+"F28.imprint","IMPRINT",EDGE,{"derivedFrom":subQ0}),-1.0]])]});}
            extrude(context, id + "F30", {"entities" : qUnion([Q0]), "depth" : 24 * mm});
        }
        {
            var Q0;
            Q0=makeQuery(id+"F1.opExtrude","CAP_FACE",FACE,{"disambiguationData":[OSD([sQuery(id+"F0.wireOp",EDGE,"E0"),sQuery(id+"F0.wireOp",EDGE,"E1"),sQuery(id+"F0.wireOp",EDGE,"E2"),sQuery(id+"F0.wireOp",EDGE,"E3"),sQuery(id+"F0.wireOp",EDGE,"E4"),sQuery(id+"F0.wireOp",EDGE,"E5"),sQuery(id+"F0.wireOp",EDGE,"E6"),sQuery(id+"F0.wireOp",EDGE,"E7"),sQuery(id+"F0.wireOp",EDGE,"E8"),sQuery(id+"F0.wireOp",EDGE,"E9"),sQuery(id+"F0.wireOp",EDGE,"E10"),sQuery(id+"F0.wireOp",EDGE,"E11"),sQuery(id+"F0.wireOp",EDGE,"E12"),sQuery(id+"F0.wireOp",EDGE,"E13"),sQuery(id+"F0.wireOp",EDGE,"E14"),sQuery(id+"F0.wireOp",EDGE,"E15"),sQuery(id+"F0.wireOp",EDGE,"E16"),sQuery(id+"F0.wireOp",EDGE,"E17"),sQuery(id+"F0.wireOp",EDGE,"E18"),sQuery(id+"F0.wireOp",EDGE,"E19"),sQuery(id+"F0.wireOp",EDGE,"E20"),sQuery(id+"F0.wireOp",EDGE,"E21"),sQuery(id+"F0.wireOp",EDGE,"E22"),sQuery(id+"F0.wireOp",EDGE,"E23"),sQuery(id+"F0.wireOp",EDGE,"E44"),sQuery(id+"F0.wireOp",EDGE,"E45"),sQuery(id+"F0.wireOp",EDGE,"E46"),sQuery(id+"F0.wireOp",EDGE,"E47"),sQuery(id+"F0.wireOp",EDGE,"E48"),sQuery(id+"F0.wireOp",EDGE,"E49"),sQuery(id+"F0.wireOp",EDGE,"E50"),sQuery(id+"F0.wireOp",EDGE,"E51"),sQuery(id+"F0.wireOp",EDGE,"E52"),sQuery(id+"F0.wireOp",EDGE,"E53"),sQuery(id+"F0.wireOp",EDGE,"E54"),sQuery(id+"F0.wireOp",EDGE,"E55"),sQuery(id+"F0.wireOp",EDGE,"E56"),sQuery(id+"F0.wireOp",EDGE,"E57"),sQuery(id+"F0.wireOp",EDGE,"E58"),sQuery(id+"F0.wireOp",EDGE,"E59"),sQuery(id+"F0.wireOp",EDGE,"E60"),sQuery(id+"F0.wireOp",EDGE,"E61"),sQuery(id+"F0.wireOp",EDGE,"E62"),sQuery(id+"F0.wireOp",EDGE,"E63"),sQuery(id+"F0.wireOp",EDGE,"E64"),sQuery(id+"F0.wireOp",EDGE,"E65"),sQuery(id+"F0.wireOp",EDGE,"E66"),sQuery(id+"F0.wireOp",EDGE,"E67"),sQuery(id+"F0.wireOp",EDGE,"E72"),sQuery(id+"F0.wireOp",EDGE,"E73"),sQuery(id+"F0.wireOp",EDGE,"E74"),sQuery(id+"F0.wireOp",EDGE,"E75")])],"isStart":false});
            var sketch = newSketch(context, id + "F31", { "sketchPlane" : qUnion([Q0])});
            skArc(sketch, "E210", {"start": v(5710.12, -945.4) * mm, "mid": v(5660.12, -895.4) * mm, "end": v(5610.12, -945.4) * mm});
            skArc(sketch, "E211", {"start": v(5610.12, -945.4) * mm, "mid": v(5560.12, -895.4) * mm, "end": v(5510.12, -945.4) * mm});
            skArc(sketch, "E212", {"start": v(4015.12, -945.4) * mm, "mid": v(3965.12, -895.4) * mm, "end": v(3915.12, -945.4) * mm});
            skArc(sketch, "E213", {"start": v(3915.12, -945.4) * mm, "mid": v(3865.12, -895.4) * mm, "end": v(3815.12, -945.4) * mm});
            skArc(sketch, "E214", {"start": v(2320.12, -945.4) * mm, "mid": v(2270.12, -895.4) * mm, "end": v(2220.12, -945.4) * mm});
            skArc(sketch, "E215", {"start": v(2220.12, -945.4) * mm, "mid": v(2170.12, -895.4) * mm, "end": v(2120.12, -945.4) * mm});
            skLineSegment(sketch, "E216", {"start": v(2120.12, -945.4) * mm, "end": v(2320.12, -945.4) * mm});
            skLineSegment(sketch, "E217", {"start": v(3815.12, -945.4) * mm, "end": v(4015.12, -945.4) * mm});
            skLineSegment(sketch, "E218", {"start": v(5510.12, -945.4) * mm, "end": v(5710.12, -945.4) * mm});
            skLineSegment(sketch, "E219", {"start": v(2165.12, -895.65) * mm, "end": v(2165.12, -825.65) * mm});
            skLineSegment(sketch, "E220", {"start": v(2165.12, -825.65) * mm, "end": v(2175.12, -825.65) * mm});
            skLineSegment(sketch, "E221", {"start": v(2175.12, -825.65) * mm, "end": v(2175.12, -895.65) * mm});
            skLineSegment(sketch, "E222", {"start": v(2265.12, -895.65) * mm, "end": v(2265.12, -825.65) * mm});
            skLineSegment(sketch, "E223", {"start": v(2265.12, -825.65) * mm, "end": v(2275.12, -825.65) * mm});
            skLineSegment(sketch, "E224", {"start": v(2275.12, -825.65) * mm, "end": v(2275.12, -895.65) * mm});
            skLineSegment(sketch, "E225", {"start": v(3860.12, -895.65) * mm, "end": v(3860.12, -825.65) * mm});
            skLineSegment(sketch, "E226", {"start": v(3860.12, -825.65) * mm, "end": v(3870.12, -825.65) * mm});
            skLineSegment(sketch, "E227", {"start": v(3870.12, -825.65) * mm, "end": v(3870.12, -895.65) * mm});
            skLineSegment(sketch, "E228", {"start": v(3960.12, -895.65) * mm, "end": v(3960.12, -825.65) * mm});
            skLineSegment(sketch, "E229", {"start": v(3960.12, -825.65) * mm, "end": v(3970.12, -825.65) * mm});
            skLineSegment(sketch, "E230", {"start": v(3970.12, -825.65) * mm, "end": v(3970.12, -895.65) * mm});
            skLineSegment(sketch, "E231", {"start": v(5555.12, -895.65) * mm, "end": v(5555.12, -825.65) * mm});
            skLineSegment(sketch, "E232", {"start": v(5555.12, -825.65) * mm, "end": v(5565.12, -825.65) * mm});
            skLineSegment(sketch, "E233", {"start": v(5565.12, -825.65) * mm, "end": v(5565.12, -895.65) * mm});
            skLineSegment(sketch, "E234", {"start": v(5655.12, -895.65) * mm, "end": v(5655.12, -825.65) * mm});
            skLineSegment(sketch, "E235", {"start": v(5655.12, -825.65) * mm, "end": v(5665.12, -825.65) * mm});
            skLineSegment(sketch, "E236", {"start": v(5665.12, -825.65) * mm, "end": v(5665.12, -895.65) * mm});
            skSolve(sketch);
        }
        {
            var Q0;
            {var subQ1=sQuery(id+"F31.wireOp",EDGE,"E215");var subQ5=makeQuery(id+"F31.imprint","INTERSECT",VERTEX,{"derivedFrom":[subQ1,sQuery(id+"F31.wireOp",EDGE,"E219")]});Q0=makeQuery(id+"F31.imprint","IMPRINT",FACE,{"disambiguationData":[TD([[makeQuery(id+"F31.imprint","IMPRINT",EDGE,{"disambiguationData":[TD([[subQ5,1.0]])],"derivedFrom":subQ1}),1.0]])]});}
            var Q1;
            {var subQ0=sQuery(id+"F31.wireOp",EDGE,"E216");var subQ1=sQuery(id+"F31.wireOp",EDGE,"E214");var subQ2=makeQuery(id+"F31.imprint","INTERSECT",VERTEX,{"derivedFrom":[subQ1,subQ0]});Q1=makeQuery(id+"F31.imprint","IMPRINT",FACE,{"disambiguationData":[TD([[makeQuery(id+"F31.imprint","IMPRINT",EDGE,{"disambiguationData":[TD([[subQ2,-1.0]])],"derivedFrom":subQ1}),1.0]])]});}
            var Q2;
            {var subQ1=sQuery(id+"F31.wireOp",EDGE,"E213");var subQ5=makeQuery(id+"F31.imprint","INTERSECT",VERTEX,{"derivedFrom":[subQ1,sQuery(id+"F31.wireOp",EDGE,"E225")]});Q2=makeQuery(id+"F31.imprint","IMPRINT",FACE,{"disambiguationData":[TD([[makeQuery(id+"F31.imprint","IMPRINT",EDGE,{"disambiguationData":[TD([[subQ5,1.0]])],"derivedFrom":subQ1}),1.0]])]});}
            var Q3;
            {var subQ0=sQuery(id+"F31.wireOp",EDGE,"E217");var subQ1=sQuery(id+"F31.wireOp",EDGE,"E212");var subQ2=makeQuery(id+"F31.imprint","INTERSECT",VERTEX,{"derivedFrom":[subQ1,subQ0]});Q3=makeQuery(id+"F31.imprint","IMPRINT",FACE,{"disambiguationData":[TD([[makeQuery(id+"F31.imprint","IMPRINT",EDGE,{"disambiguationData":[TD([[subQ2,-1.0]])],"derivedFrom":subQ1}),1.0]])]});}
            var Q4;
            {var subQ0=sQuery(id+"F31.wireOp",EDGE,"E218");var subQ1=sQuery(id+"F31.wireOp",EDGE,"E210");var subQ2=makeQuery(id+"F31.imprint","INTERSECT",VERTEX,{"derivedFrom":[subQ1,subQ0]});Q4=makeQuery(id+"F31.imprint","IMPRINT",FACE,{"disambiguationData":[TD([[makeQuery(id+"F31.imprint","IMPRINT",EDGE,{"disambiguationData":[TD([[subQ2,-1.0]])],"derivedFrom":subQ1}),1.0]])]});}
            var Q5;
            {var subQ1=sQuery(id+"F31.wireOp",EDGE,"E211");var subQ5=makeQuery(id+"F31.imprint","INTERSECT",VERTEX,{"derivedFrom":[subQ1,sQuery(id+"F31.wireOp",EDGE,"E231")]});Q5=makeQuery(id+"F31.imprint","IMPRINT",FACE,{"disambiguationData":[TD([[makeQuery(id+"F31.imprint","IMPRINT",EDGE,{"disambiguationData":[TD([[subQ5,1.0]])],"derivedFrom":subQ1}),1.0]])]});}
            extrude(context, id + "F32", {"entities" : qUnion([Q0, Q1, Q2, Q3, Q4, Q5]), "depth" : 25 * mm});
        }
        {
            var Q0;
            {var subQ0=sQuery(id+"F31.wireOp",EDGE,"E219");Q0=makeQuery(id+"F31.imprint","IMPRINT",FACE,{"disambiguationData":[TD([[makeQuery(id+"F31.imprint","IMPRINT",EDGE,{"derivedFrom":subQ0}),-1.0]])]});}
            var Q1;
            {var subQ0=sQuery(id+"F31.wireOp",EDGE,"E222");Q1=makeQuery(id+"F31.imprint","IMPRINT",FACE,{"disambiguationData":[TD([[makeQuery(id+"F31.imprint","IMPRINT",EDGE,{"derivedFrom":subQ0}),-1.0]])]});}
            var Q2;
            {var subQ0=sQuery(id+"F31.wireOp",EDGE,"E225");Q2=makeQuery(id+"F31.imprint","IMPRINT",FACE,{"disambiguationData":[TD([[makeQuery(id+"F31.imprint","IMPRINT",EDGE,{"derivedFrom":subQ0}),-1.0]])]});}
            var Q3;
            {var subQ0=sQuery(id+"F31.wireOp",EDGE,"E228");Q3=makeQuery(id+"F31.imprint","IMPRINT",FACE,{"disambiguationData":[TD([[makeQuery(id+"F31.imprint","IMPRINT",EDGE,{"derivedFrom":subQ0}),-1.0]])]});}
            var Q4;
            {var subQ0=sQuery(id+"F31.wireOp",EDGE,"E231");Q4=makeQuery(id+"F31.imprint","IMPRINT",FACE,{"disambiguationData":[TD([[makeQuery(id+"F31.imprint","IMPRINT",EDGE,{"derivedFrom":subQ0}),-1.0]])]});}
            var Q5;
            {var subQ0=sQuery(id+"F31.wireOp",EDGE,"E234");Q5=makeQuery(id+"F31.imprint","IMPRINT",FACE,{"disambiguationData":[TD([[makeQuery(id+"F31.imprint","IMPRINT",EDGE,{"derivedFrom":subQ0}),-1.0]])]});}
            extrude(context, id + "F33", {"entities" : qUnion([Q0, Q1, Q2, Q3, Q4, Q5]), "depth" : 24 * mm});
        }
        {
            var Q0;
            Q0=makeQuery(id+"F1.opExtrude","CAP_FACE",FACE,{"disambiguationData":[OSD([sQuery(id+"F0.wireOp",EDGE,"E0"),sQuery(id+"F0.wireOp",EDGE,"E1"),sQuery(id+"F0.wireOp",EDGE,"E2"),sQuery(id+"F0.wireOp",EDGE,"E3"),sQuery(id+"F0.wireOp",EDGE,"E4"),sQuery(id+"F0.wireOp",EDGE,"E5"),sQuery(id+"F0.wireOp",EDGE,"E6"),sQuery(id+"F0.wireOp",EDGE,"E7"),sQuery(id+"F0.wireOp",EDGE,"E8"),sQuery(id+"F0.wireOp",EDGE,"E9"),sQuery(id+"F0.wireOp",EDGE,"E10"),sQuery(id+"F0.wireOp",EDGE,"E11"),sQuery(id+"F0.wireOp",EDGE,"E12"),sQuery(id+"F0.wireOp",EDGE,"E13"),sQuery(id+"F0.wireOp",EDGE,"E14"),sQuery(id+"F0.wireOp",EDGE,"E15"),sQuery(id+"F0.wireOp",EDGE,"E16"),sQuery(id+"F0.wireOp",EDGE,"E17"),sQuery(id+"F0.wireOp",EDGE,"E18"),sQuery(id+"F0.wireOp",EDGE,"E19"),sQuery(id+"F0.wireOp",EDGE,"E20"),sQuery(id+"F0.wireOp",EDGE,"E21"),sQuery(id+"F0.wireOp",EDGE,"E22"),sQuery(id+"F0.wireOp",EDGE,"E23"),sQuery(id+"F0.wireOp",EDGE,"E44"),sQuery(id+"F0.wireOp",EDGE,"E45"),sQuery(id+"F0.wireOp",EDGE,"E46"),sQuery(id+"F0.wireOp",EDGE,"E47"),sQuery(id+"F0.wireOp",EDGE,"E48"),sQuery(id+"F0.wireOp",EDGE,"E49"),sQuery(id+"F0.wireOp",EDGE,"E50"),sQuery(id+"F0.wireOp",EDGE,"E51"),sQuery(id+"F0.wireOp",EDGE,"E52"),sQuery(id+"F0.wireOp",EDGE,"E53"),sQuery(id+"F0.wireOp",EDGE,"E54"),sQuery(id+"F0.wireOp",EDGE,"E55"),sQuery(id+"F0.wireOp",EDGE,"E56"),sQuery(id+"F0.wireOp",EDGE,"E57"),sQuery(id+"F0.wireOp",EDGE,"E58"),sQuery(id+"F0.wireOp",EDGE,"E59"),sQuery(id+"F0.wireOp",EDGE,"E60"),sQuery(id+"F0.wireOp",EDGE,"E61"),sQuery(id+"F0.wireOp",EDGE,"E62"),sQuery(id+"F0.wireOp",EDGE,"E63"),sQuery(id+"F0.wireOp",EDGE,"E64"),sQuery(id+"F0.wireOp",EDGE,"E65"),sQuery(id+"F0.wireOp",EDGE,"E66"),sQuery(id+"F0.wireOp",EDGE,"E67"),sQuery(id+"F0.wireOp",EDGE,"E72"),sQuery(id+"F0.wireOp",EDGE,"E73"),sQuery(id+"F0.wireOp",EDGE,"E74"),sQuery(id+"F0.wireOp",EDGE,"E75")])],"isStart":false});
            var sketch = newSketch(context, id + "F34", { "sketchPlane" : qUnion([Q0])});
            skArc(sketch, "E237", {"start": v(-784.88, 239.6) * mm, "mid": v(-834.88, 189.6) * mm, "end": v(-784.88, 139.6) * mm});
            skLineSegment(sketch, "E238", {"start": v(-784.88, 239.6) * mm, "end": v(-784.88, 139.6) * mm});
            skLineSegment(sketch, "E239", {"start": v(-834.63, 194.6) * mm, "end": v(-904.63, 194.6) * mm});
            skLineSegment(sketch, "E240", {"start": v(-904.63, 194.6) * mm, "end": v(-904.63, 184.6) * mm});
            skLineSegment(sketch, "E241", {"start": v(-904.63, 184.6) * mm, "end": v(-834.63, 184.6) * mm});
            skSolve(sketch);
        }
        {
            var Q0;
            {var subQ0=sQuery(id+"F34.wireOp",EDGE,"E238");Q0=makeQuery(id+"F34.imprint","IMPRINT",FACE,{"disambiguationData":[TD([[makeQuery(id+"F34.imprint","IMPRINT",EDGE,{"derivedFrom":subQ0}),-1.0]])]});}
            extrude(context, id + "F35", {"entities" : qUnion([Q0]), "depth" : 25 * mm});
        }
        {
            var Q0;
            {var subQ0=sQuery(id+"F34.wireOp",EDGE,"E239");Q0=makeQuery(id+"F34.imprint","IMPRINT",FACE,{"disambiguationData":[TD([[makeQuery(id+"F34.imprint","IMPRINT",EDGE,{"derivedFrom":subQ0}),1.0]])]});}
            extrude(context, id + "F36", {"entities" : qUnion([Q0]), "depth" : 24 * mm});
        }
    });
